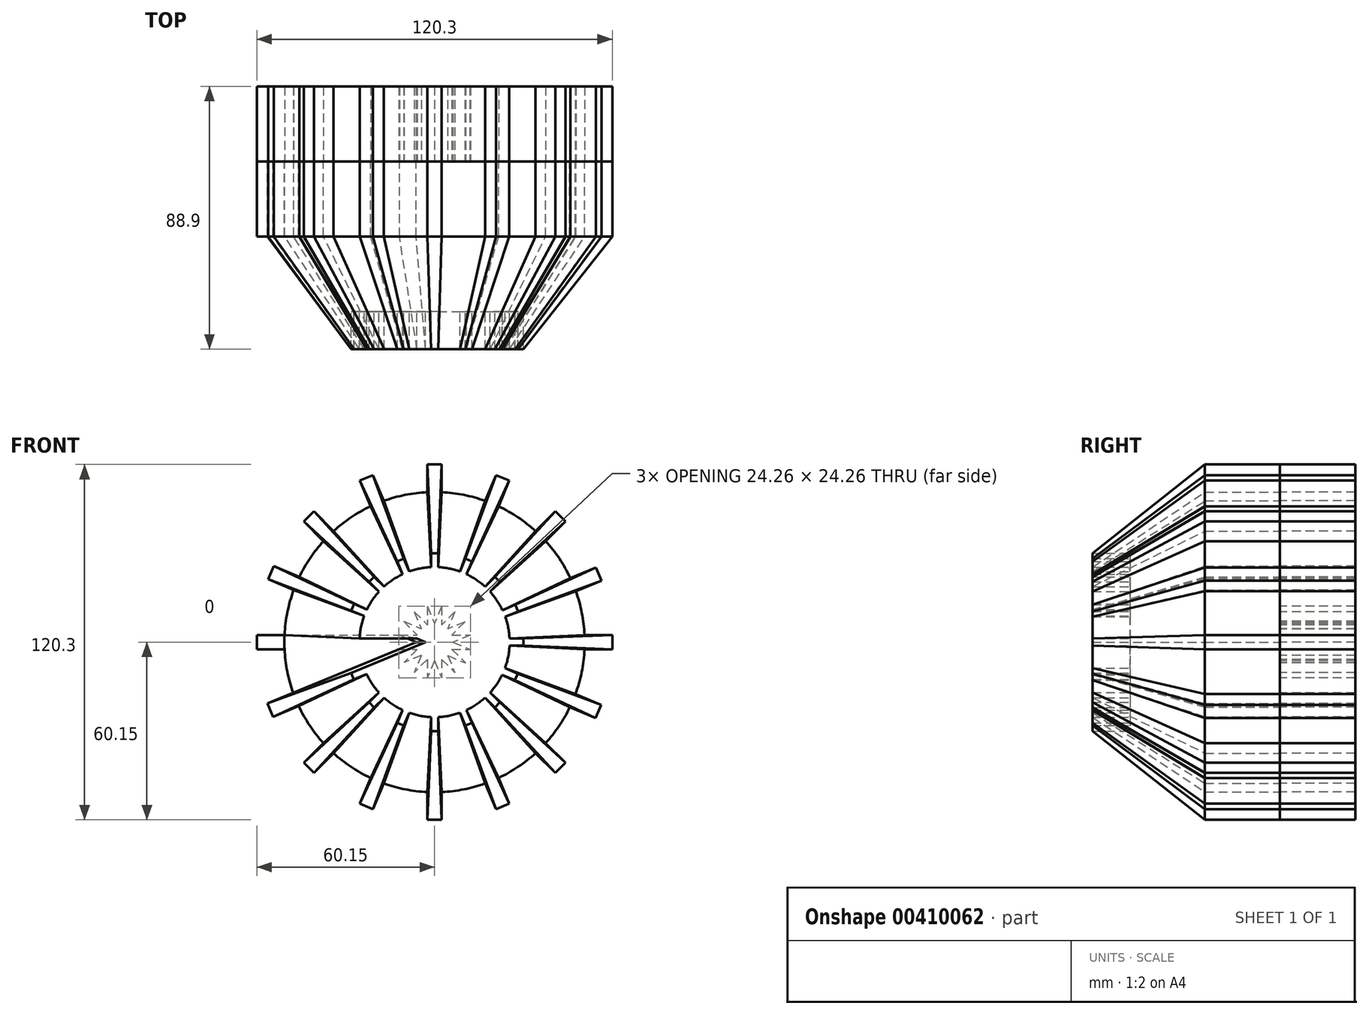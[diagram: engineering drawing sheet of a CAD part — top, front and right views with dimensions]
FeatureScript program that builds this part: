
annotation { "Feature Type Name" : "Feature", "Feature Type Description" : "" }
export const myFeature = defineFeature(function(context is Context, id is Id, definition is map)
    precondition{}
    {
        {
            var Q0;
            Q0=qCreatedBy(makeId("Front.planeOp"),FACE);
            var sketch = newSketch(context, id + "F0", { "sketchPlane" : qUnion([Q0])});
            skCircle(sketch, "E0", {"center": v(0, 0) * mm, "radius": 50.8 * mm});
            skLineSegment(sketch, "E1.bottom", {"start": v(-60.15, 2.41) * mm, "end": v(60.15, 2.41) * mm});
            skLineSegment(sketch, "E1.top", {"start": v(-60.15, -2.41) * mm, "end": v(60.15, -2.41) * mm});
            skLineSegment(sketch, "E1.left", {"start": v(-60.15, 2.41) * mm, "end": v(-60.15, -2.41) * mm});
            skLineSegment(sketch, "E1.right", {"start": v(60.15, 2.41) * mm, "end": v(60.15, -2.41) * mm});
            skLineSegment(sketch, "E2.bottom", {"start": v(2.41, 60.15) * mm, "end": v(2.41, -60.15) * mm});
            skLineSegment(sketch, "E2.top", {"start": v(-2.41, 60.15) * mm, "end": v(-2.41, -60.15) * mm});
            skLineSegment(sketch, "E2.left", {"start": v(2.41, 60.15) * mm, "end": v(-2.41, 60.15) * mm});
            skLineSegment(sketch, "E2.right", {"start": v(2.41, -60.15) * mm, "end": v(-2.41, -60.15) * mm});
            skLineSegment(sketch, "E3.bottom", {"start": v(-20.79, 56.5) * mm, "end": v(25.25, -54.65) * mm});
            skLineSegment(sketch, "E3.top", {"start": v(-25.25, 54.65) * mm, "end": v(20.79, -56.5) * mm});
            skLineSegment(sketch, "E3.left", {"start": v(-20.79, 56.5) * mm, "end": v(-25.25, 54.65) * mm});
            skLineSegment(sketch, "E3.right", {"start": v(25.25, -54.65) * mm, "end": v(20.79, -56.5) * mm});
            skLineSegment(sketch, "E4.bottom", {"start": v(-40.82, 44.24) * mm, "end": v(44.24, -40.82) * mm});
            skLineSegment(sketch, "E4.top", {"start": v(-44.24, 40.82) * mm, "end": v(40.82, -44.24) * mm});
            skLineSegment(sketch, "E4.left", {"start": v(-40.82, 44.24) * mm, "end": v(-44.24, 40.82) * mm});
            skLineSegment(sketch, "E4.right", {"start": v(44.24, -40.82) * mm, "end": v(40.82, -44.24) * mm});
            skLineSegment(sketch, "E5.bottom", {"start": v(-54.42, 25.73) * mm, "end": v(56.3, -21.28) * mm});
            skLineSegment(sketch, "E5.top", {"start": v(-56.3, 21.28) * mm, "end": v(54.42, -25.73) * mm});
            skLineSegment(sketch, "E5.left", {"start": v(-54.42, 25.73) * mm, "end": v(-56.3, 21.28) * mm});
            skLineSegment(sketch, "E5.right", {"start": v(56.3, -21.28) * mm, "end": v(54.42, -25.73) * mm});
            skLineSegment(sketch, "E6.bottom", {"start": v(56.5, 20.8) * mm, "end": v(-54.64, -25.25) * mm});
            skLineSegment(sketch, "E6.top", {"start": v(54.64, 25.25) * mm, "end": v(-56.5, -20.8) * mm});
            skLineSegment(sketch, "E6.left", {"start": v(56.5, 20.8) * mm, "end": v(54.64, 25.25) * mm});
            skLineSegment(sketch, "E6.right", {"start": v(-54.64, -25.25) * mm, "end": v(-56.5, -20.8) * mm});
            skLineSegment(sketch, "E7.bottom", {"start": v(44.24, 40.82) * mm, "end": v(-40.82, -44.24) * mm});
            skLineSegment(sketch, "E7.top", {"start": v(40.82, 44.24) * mm, "end": v(-44.24, -40.82) * mm});
            skLineSegment(sketch, "E7.left", {"start": v(44.24, 40.82) * mm, "end": v(40.82, 44.24) * mm});
            skLineSegment(sketch, "E7.right", {"start": v(-40.82, -44.24) * mm, "end": v(-44.24, -40.82) * mm});
            skLineSegment(sketch, "E8.bottom", {"start": v(25.25, 54.65) * mm, "end": v(-20.79, -56.5) * mm});
            skLineSegment(sketch, "E8.top", {"start": v(20.79, 56.5) * mm, "end": v(-25.25, -54.65) * mm});
            skLineSegment(sketch, "E8.left", {"start": v(25.25, 54.65) * mm, "end": v(20.79, 56.5) * mm});
            skLineSegment(sketch, "E8.right", {"start": v(-20.79, -56.5) * mm, "end": v(-25.25, -54.65) * mm});
            skSolve(sketch);
        }
        {
            var Q0;
            Q0=qCreatedBy(makeId("Front.planeOp"),FACE);
            cPlane(context, id + "F1", {"entities" : qUnion([Q0]), "cplaneType" : CPlaneType.OFFSET, "offset" : 60.16 * mm, "width" : 152.4 * mm, "height" : 152.4 * mm});
        }
        {
            var Q0;
            {var subQ0=sQuery(id+"F0.wireOp",EDGE,"E7.bottom");var subQ1=sQuery(id+"F0.wireOp",EDGE,"E0");var subQ2=makeQuery(id+"F0.imprint","INTERSECT",VERTEX,{"disambiguationData":[OD(1.0)],"derivedFrom":[subQ1,subQ0]});Q0=makeQuery(id+"F0.imprint","IMPRINT",FACE,{"disambiguationData":[TD([[makeQuery(id+"F0.imprint","IMPRINT",EDGE,{"disambiguationData":[TD([[subQ2,-1.0]])],"derivedFrom":subQ1}),1.0]])]});}
            var Q1;
            {var subQ0=sQuery(id+"F0.wireOp",EDGE,"E7.top");var subQ1=sQuery(id+"F0.wireOp",EDGE,"E2.bottom");var subQ2=makeQuery(id+"F0.imprint","INTERSECT",VERTEX,{"derivedFrom":[subQ1,subQ0]});Q1=makeQuery(id+"F0.imprint","IMPRINT",FACE,{"disambiguationData":[TD([[makeQuery(id+"F0.imprint","IMPRINT",EDGE,{"disambiguationData":[TD([[subQ2,-1.0]])],"derivedFrom":subQ1}),1.0]])]});}
            var Q2;
            {var subQ3=sQuery(id+"F0.wireOp",EDGE,"E8.top");var subQ6=sQuery(id+"F0.wireOp",EDGE,"E0");var subQ9=makeQuery(id+"F0.imprint","INTERSECT",VERTEX,{"disambiguationData":[OD(1.0)],"derivedFrom":[subQ6,subQ3]});Q2=makeQuery(id+"F0.imprint","IMPRINT",FACE,{"disambiguationData":[TD([[makeQuery(id+"F0.imprint","IMPRINT",EDGE,{"disambiguationData":[TD([[subQ9,-1.0]])],"derivedFrom":subQ6}),1.0]])]});}
            var Q3;
            {var subQ0=sQuery(id+"F0.wireOp",EDGE,"E3.bottom");var subQ1=sQuery(id+"F0.wireOp",EDGE,"E0");var subQ2=makeQuery(id+"F0.imprint","INTERSECT",VERTEX,{"disambiguationData":[OD(1.0)],"derivedFrom":[subQ1,subQ0]});Q3=makeQuery(id+"F0.imprint","IMPRINT",FACE,{"disambiguationData":[TD([[makeQuery(id+"F0.imprint","IMPRINT",EDGE,{"disambiguationData":[TD([[subQ2,-1.0]])],"derivedFrom":subQ1}),1.0]])]});}
            var Q4;
            {var subQ1=sQuery(id+"F0.wireOp",EDGE,"E0");var subQ7=sQuery(id+"F0.wireOp",EDGE,"E4.top");var subQ9=makeQuery(id+"F0.imprint","INTERSECT",VERTEX,{"disambiguationData":[OD(1.0)],"derivedFrom":[subQ1,subQ7]});Q4=makeQuery(id+"F0.imprint","IMPRINT",FACE,{"disambiguationData":[TD([[makeQuery(id+"F0.imprint","IMPRINT",EDGE,{"disambiguationData":[TD([[subQ9,-1.0]])],"derivedFrom":subQ1}),1.0]])]});}
            var Q5;
            {var subQ0=sQuery(id+"F0.wireOp",EDGE,"E8.bottom");var subQ1=sQuery(id+"F0.wireOp",EDGE,"E0");var subQ2=makeQuery(id+"F0.imprint","INTERSECT",VERTEX,{"disambiguationData":[OD(1.0)],"derivedFrom":[subQ1,subQ0]});Q5=makeQuery(id+"F0.imprint","IMPRINT",FACE,{"disambiguationData":[TD([[makeQuery(id+"F0.imprint","IMPRINT",EDGE,{"disambiguationData":[TD([[subQ2,-1.0]])],"derivedFrom":subQ1}),1.0]])]});}
            var Q6;
            {var subQ5=sQuery(id+"F0.wireOp",EDGE,"E2.top");var subQ6=sQuery(id+"F0.wireOp",EDGE,"E0");var subQ7=makeQuery(id+"F0.imprint","INTERSECT",VERTEX,{"disambiguationData":[OD(1.0)],"derivedFrom":[subQ6,subQ5]});Q6=makeQuery(id+"F0.imprint","IMPRINT",FACE,{"disambiguationData":[TD([[makeQuery(id+"F0.imprint","IMPRINT",EDGE,{"disambiguationData":[TD([[subQ7,-1.0]])],"derivedFrom":subQ6}),1.0]])]});}
            var Q7;
            {var subQ0=sQuery(id+"F0.wireOp",EDGE,"E4.bottom");var subQ1=sQuery(id+"F0.wireOp",EDGE,"E0");var subQ2=makeQuery(id+"F0.imprint","INTERSECT",VERTEX,{"disambiguationData":[OD(1.0)],"derivedFrom":[subQ1,subQ0]});Q7=makeQuery(id+"F0.imprint","IMPRINT",FACE,{"disambiguationData":[TD([[makeQuery(id+"F0.imprint","IMPRINT",EDGE,{"disambiguationData":[TD([[subQ2,-1.0]])],"derivedFrom":subQ1}),1.0]])]});}
            var Q8;
            {var subQ1=sQuery(id+"F0.wireOp",EDGE,"E0");var subQ7=sQuery(id+"F0.wireOp",EDGE,"E5.top");var subQ9=makeQuery(id+"F0.imprint","INTERSECT",VERTEX,{"disambiguationData":[OD(1.0)],"derivedFrom":[subQ1,subQ7]});Q8=makeQuery(id+"F0.imprint","IMPRINT",FACE,{"disambiguationData":[TD([[makeQuery(id+"F0.imprint","IMPRINT",EDGE,{"disambiguationData":[TD([[subQ9,-1.0]])],"derivedFrom":subQ1}),1.0]])]});}
            var Q9;
            {var subQ0=sQuery(id+"F0.wireOp",EDGE,"E6.bottom");var subQ1=sQuery(id+"F0.wireOp",EDGE,"E2.top");var subQ2=makeQuery(id+"F0.imprint","INTERSECT",VERTEX,{"derivedFrom":[subQ1,subQ0]});Q9=makeQuery(id+"F0.imprint","IMPRINT",FACE,{"disambiguationData":[TD([[makeQuery(id+"F0.imprint","IMPRINT",EDGE,{"disambiguationData":[TD([[subQ2,-1.0]])],"derivedFrom":subQ1}),-1.0]])]});}
            var Q10;
            {var subQ0=sQuery(id+"F0.wireOp",EDGE,"E2.bottom");var subQ1=sQuery(id+"F0.wireOp",EDGE,"E0");var subQ2=makeQuery(id+"F0.imprint","INTERSECT",VERTEX,{"disambiguationData":[OD(1.0)],"derivedFrom":[subQ1,subQ0]});Q10=makeQuery(id+"F0.imprint","IMPRINT",FACE,{"disambiguationData":[TD([[makeQuery(id+"F0.imprint","IMPRINT",EDGE,{"disambiguationData":[TD([[subQ2,-1.0]])],"derivedFrom":subQ1}),1.0]])]});}
            var Q11;
            {var subQ0=sQuery(id+"F0.wireOp",EDGE,"E3.top");var subQ1=sQuery(id+"F0.wireOp",EDGE,"E0");var subQ2=makeQuery(id+"F0.imprint","INTERSECT",VERTEX,{"disambiguationData":[OD(1.0)],"derivedFrom":[subQ1,subQ0]});Q11=makeQuery(id+"F0.imprint","IMPRINT",FACE,{"disambiguationData":[TD([[makeQuery(id+"F0.imprint","IMPRINT",EDGE,{"disambiguationData":[TD([[subQ2,-1.0]])],"derivedFrom":subQ1}),1.0]])]});}
            var Q12;
            {var subQ0=sQuery(id+"F0.wireOp",EDGE,"E6.bottom");var subQ1=sQuery(id+"F0.wireOp",EDGE,"E0");var subQ2=makeQuery(id+"F0.imprint","INTERSECT",VERTEX,{"disambiguationData":[OD(0.0)],"derivedFrom":[subQ1,subQ0]});Q12=makeQuery(id+"F0.imprint","IMPRINT",FACE,{"disambiguationData":[TD([[makeQuery(id+"F0.imprint","IMPRINT",EDGE,{"disambiguationData":[TD([[subQ2,1.0]])],"derivedFrom":subQ1}),1.0]])]});}
            var Q13;
            {var subQ1=sQuery(id+"F0.wireOp",EDGE,"E0");var subQ5=sQuery(id+"F0.wireOp",EDGE,"E6.bottom");var subQ6=makeQuery(id+"F0.imprint","INTERSECT",VERTEX,{"disambiguationData":[OD(0.0)],"derivedFrom":[subQ1,subQ5]});Q13=makeQuery(id+"F0.imprint","IMPRINT",FACE,{"disambiguationData":[TD([[makeQuery(id+"F0.imprint","IMPRINT",EDGE,{"disambiguationData":[TD([[subQ6,-1.0]])],"derivedFrom":subQ1}),1.0]])]});}
            var Q14;
            {var subQ0=sQuery(id+"F0.wireOp",EDGE,"E6.top");var subQ1=sQuery(id+"F0.wireOp",EDGE,"E0");var subQ2=makeQuery(id+"F0.imprint","INTERSECT",VERTEX,{"disambiguationData":[OD(0.0)],"derivedFrom":[subQ1,subQ0]});Q14=makeQuery(id+"F0.imprint","IMPRINT",FACE,{"disambiguationData":[TD([[makeQuery(id+"F0.imprint","IMPRINT",EDGE,{"disambiguationData":[TD([[subQ2,-1.0]])],"derivedFrom":subQ1}),1.0]])]});}
            var Q15;
            {var subQ0=sQuery(id+"F0.wireOp",EDGE,"E7.bottom");var subQ1=sQuery(id+"F0.wireOp",EDGE,"E0");var subQ2=makeQuery(id+"F0.imprint","INTERSECT",VERTEX,{"disambiguationData":[OD(0.0)],"derivedFrom":[subQ1,subQ0]});Q15=makeQuery(id+"F0.imprint","IMPRINT",FACE,{"disambiguationData":[TD([[makeQuery(id+"F0.imprint","IMPRINT",EDGE,{"disambiguationData":[TD([[subQ2,-1.0]])],"derivedFrom":subQ1}),1.0]])]});}
            var Q16;
            {var subQ0=sQuery(id+"F0.wireOp",EDGE,"E5.top");var subQ1=sQuery(id+"F0.wireOp",EDGE,"E2.bottom");var subQ2=makeQuery(id+"F0.imprint","INTERSECT",VERTEX,{"derivedFrom":[subQ1,subQ0]});Q16=makeQuery(id+"F0.imprint","IMPRINT",FACE,{"disambiguationData":[TD([[makeQuery(id+"F0.imprint","IMPRINT",EDGE,{"disambiguationData":[TD([[subQ2,-1.0]])],"derivedFrom":subQ1}),1.0]])]});}
            var Q17;
            {var subQ0=sQuery(id+"F0.wireOp",EDGE,"E7.top");var subQ1=sQuery(id+"F0.wireOp",EDGE,"E0");var subQ2=makeQuery(id+"F0.imprint","INTERSECT",VERTEX,{"disambiguationData":[OD(0.0)],"derivedFrom":[subQ1,subQ0]});Q17=makeQuery(id+"F0.imprint","IMPRINT",FACE,{"disambiguationData":[TD([[makeQuery(id+"F0.imprint","IMPRINT",EDGE,{"disambiguationData":[TD([[subQ2,-1.0]])],"derivedFrom":subQ1}),1.0]])]});}
            var Q18;
            {var subQ3=sQuery(id+"F0.wireOp",EDGE,"E8.bottom");var subQ5=sQuery(id+"F0.wireOp",EDGE,"E0");var subQ6=makeQuery(id+"F0.imprint","INTERSECT",VERTEX,{"disambiguationData":[OD(0.0)],"derivedFrom":[subQ5,subQ3]});Q18=makeQuery(id+"F0.imprint","IMPRINT",FACE,{"disambiguationData":[TD([[makeQuery(id+"F0.imprint","IMPRINT",EDGE,{"disambiguationData":[TD([[subQ6,-1.0]])],"derivedFrom":subQ5}),1.0]])]});}
            var Q19;
            {var subQ0=sQuery(id+"F0.wireOp",EDGE,"E8.top");var subQ1=sQuery(id+"F0.wireOp",EDGE,"E0");var subQ2=makeQuery(id+"F0.imprint","INTERSECT",VERTEX,{"disambiguationData":[OD(0.0)],"derivedFrom":[subQ1,subQ0]});Q19=makeQuery(id+"F0.imprint","IMPRINT",FACE,{"disambiguationData":[TD([[makeQuery(id+"F0.imprint","IMPRINT",EDGE,{"disambiguationData":[TD([[subQ2,-1.0]])],"derivedFrom":subQ1}),1.0]])]});}
            var Q20;
            {var subQ0=sQuery(id+"F0.wireOp",EDGE,"E7.bottom");var subQ1=sQuery(id+"F0.wireOp",EDGE,"E1.bottom");var subQ2=makeQuery(id+"F0.imprint","INTERSECT",VERTEX,{"derivedFrom":[subQ1,subQ0]});Q20=makeQuery(id+"F0.imprint","IMPRINT",FACE,{"disambiguationData":[TD([[makeQuery(id+"F0.imprint","IMPRINT",EDGE,{"disambiguationData":[TD([[subQ2,-1.0]])],"derivedFrom":subQ1}),-1.0]])]});}
            var Q21;
            {var subQ5=sQuery(id+"F0.wireOp",EDGE,"E2.bottom");var subQ6=sQuery(id+"F0.wireOp",EDGE,"E0");var subQ7=makeQuery(id+"F0.imprint","INTERSECT",VERTEX,{"disambiguationData":[OD(0.0)],"derivedFrom":[subQ6,subQ5]});Q21=makeQuery(id+"F0.imprint","IMPRINT",FACE,{"disambiguationData":[TD([[makeQuery(id+"F0.imprint","IMPRINT",EDGE,{"disambiguationData":[TD([[subQ7,-1.0]])],"derivedFrom":subQ6}),1.0]])]});}
            var Q22;
            {var subQ0=sQuery(id+"F0.wireOp",EDGE,"E2.top");var subQ1=sQuery(id+"F0.wireOp",EDGE,"E0");var subQ2=makeQuery(id+"F0.imprint","INTERSECT",VERTEX,{"disambiguationData":[OD(0.0)],"derivedFrom":[subQ1,subQ0]});Q22=makeQuery(id+"F0.imprint","IMPRINT",FACE,{"disambiguationData":[TD([[makeQuery(id+"F0.imprint","IMPRINT",EDGE,{"disambiguationData":[TD([[subQ2,-1.0]])],"derivedFrom":subQ1}),1.0]])]});}
            var Q23;
            {var subQ0=sQuery(id+"F0.wireOp",EDGE,"E6.top");var subQ1=sQuery(id+"F0.wireOp",EDGE,"E1.top");var subQ2=makeQuery(id+"F0.imprint","INTERSECT",VERTEX,{"derivedFrom":[subQ1,subQ0]});Q23=makeQuery(id+"F0.imprint","IMPRINT",FACE,{"disambiguationData":[TD([[makeQuery(id+"F0.imprint","IMPRINT",EDGE,{"disambiguationData":[TD([[subQ2,-1.0]])],"derivedFrom":subQ1}),1.0]])]});}
            var Q24;
            {var subQ0=sQuery(id+"F0.wireOp",EDGE,"E3.bottom");var subQ1=sQuery(id+"F0.wireOp",EDGE,"E0");var subQ2=makeQuery(id+"F0.imprint","INTERSECT",VERTEX,{"disambiguationData":[OD(0.0)],"derivedFrom":[subQ1,subQ0]});Q24=makeQuery(id+"F0.imprint","IMPRINT",FACE,{"disambiguationData":[TD([[makeQuery(id+"F0.imprint","IMPRINT",EDGE,{"disambiguationData":[TD([[subQ2,-1.0]])],"derivedFrom":subQ1}),1.0]])]});}
            var Q25;
            {var subQ0=sQuery(id+"F0.wireOp",EDGE,"E3.top");var subQ1=sQuery(id+"F0.wireOp",EDGE,"E0");var subQ2=makeQuery(id+"F0.imprint","INTERSECT",VERTEX,{"disambiguationData":[OD(0.0)],"derivedFrom":[subQ1,subQ0]});Q25=makeQuery(id+"F0.imprint","IMPRINT",FACE,{"disambiguationData":[TD([[makeQuery(id+"F0.imprint","IMPRINT",EDGE,{"disambiguationData":[TD([[subQ2,-1.0]])],"derivedFrom":subQ1}),1.0]])]});}
            var Q26;
            {var subQ1=sQuery(id+"F0.wireOp",EDGE,"E0");var subQ5=sQuery(id+"F0.wireOp",EDGE,"E4.bottom");var subQ9=makeQuery(id+"F0.imprint","INTERSECT",VERTEX,{"disambiguationData":[OD(0.0)],"derivedFrom":[subQ1,subQ5]});Q26=makeQuery(id+"F0.imprint","IMPRINT",FACE,{"disambiguationData":[TD([[makeQuery(id+"F0.imprint","IMPRINT",EDGE,{"disambiguationData":[TD([[subQ9,-1.0]])],"derivedFrom":subQ1}),1.0]])]});}
            var Q27;
            {var subQ0=sQuery(id+"F0.wireOp",EDGE,"E4.bottom");var subQ1=sQuery(id+"F0.wireOp",EDGE,"E2.top");var subQ2=makeQuery(id+"F0.imprint","INTERSECT",VERTEX,{"derivedFrom":[subQ1,subQ0]});Q27=makeQuery(id+"F0.imprint","IMPRINT",FACE,{"disambiguationData":[TD([[makeQuery(id+"F0.imprint","IMPRINT",EDGE,{"disambiguationData":[TD([[subQ2,-1.0]])],"derivedFrom":subQ1}),-1.0]])]});}
            var Q28;
            {var subQ0=sQuery(id+"F0.wireOp",EDGE,"E3.bottom");var subQ1=sQuery(id+"F0.wireOp",EDGE,"E1.top");var subQ2=makeQuery(id+"F0.imprint","INTERSECT",VERTEX,{"derivedFrom":[subQ1,subQ0]});Q28=makeQuery(id+"F0.imprint","IMPRINT",FACE,{"disambiguationData":[TD([[makeQuery(id+"F0.imprint","IMPRINT",EDGE,{"disambiguationData":[TD([[subQ2,-1.0]])],"derivedFrom":subQ1}),-1.0]])]});}
            var Q29;
            {var subQ0=sQuery(id+"F0.wireOp",EDGE,"E7.top");var subQ1=sQuery(id+"F0.wireOp",EDGE,"E1.top");var subQ2=makeQuery(id+"F0.imprint","INTERSECT",VERTEX,{"derivedFrom":[subQ1,subQ0]});Q29=makeQuery(id+"F0.imprint","IMPRINT",FACE,{"disambiguationData":[TD([[makeQuery(id+"F0.imprint","IMPRINT",EDGE,{"disambiguationData":[TD([[subQ2,-1.0]])],"derivedFrom":subQ1}),-1.0]])]});}
            var Q30;
            {var subQ0=sQuery(id+"F0.wireOp",EDGE,"E5.bottom");var subQ1=sQuery(id+"F0.wireOp",EDGE,"E0");var subQ2=makeQuery(id+"F0.imprint","INTERSECT",VERTEX,{"disambiguationData":[OD(0.0)],"derivedFrom":[subQ1,subQ0]});Q30=makeQuery(id+"F0.imprint","IMPRINT",FACE,{"disambiguationData":[TD([[makeQuery(id+"F0.imprint","IMPRINT",EDGE,{"disambiguationData":[TD([[subQ2,-1.0]])],"derivedFrom":subQ1}),1.0]])]});}
            var Q31;
            {var subQ0=sQuery(id+"F0.wireOp",EDGE,"E4.top");var subQ1=sQuery(id+"F0.wireOp",EDGE,"E0");var subQ2=makeQuery(id+"F0.imprint","INTERSECT",VERTEX,{"disambiguationData":[OD(0.0)],"derivedFrom":[subQ1,subQ0]});Q31=makeQuery(id+"F0.imprint","IMPRINT",FACE,{"disambiguationData":[TD([[makeQuery(id+"F0.imprint","IMPRINT",EDGE,{"disambiguationData":[TD([[subQ2,-1.0]])],"derivedFrom":subQ1}),1.0]])]});}
            var Q32;
            {var subQ5=sQuery(id+"F0.wireOp",EDGE,"E1.right");Q32=makeQuery(id+"F0.imprint","IMPRINT",FACE,{"disambiguationData":[TD([[makeQuery(id+"F0.imprint","IMPRINT",EDGE,{"derivedFrom":subQ5}),-1.0]])]});}
            var Q33;
            {var subQ5=sQuery(id+"F0.wireOp",EDGE,"E4.right");Q33=makeQuery(id+"F0.imprint","IMPRINT",FACE,{"disambiguationData":[TD([[makeQuery(id+"F0.imprint","IMPRINT",EDGE,{"derivedFrom":subQ5}),-1.0]])]});}
            var Q34;
            {var subQ5=sQuery(id+"F0.wireOp",EDGE,"E5.right");Q34=makeQuery(id+"F0.imprint","IMPRINT",FACE,{"disambiguationData":[TD([[makeQuery(id+"F0.imprint","IMPRINT",EDGE,{"derivedFrom":subQ5}),-1.0]])]});}
            var Q35;
            {var subQ5=sQuery(id+"F0.wireOp",EDGE,"E6.left");Q35=makeQuery(id+"F0.imprint","IMPRINT",FACE,{"disambiguationData":[TD([[makeQuery(id+"F0.imprint","IMPRINT",EDGE,{"derivedFrom":subQ5}),1.0]])]});}
            var Q36;
            {var subQ5=sQuery(id+"F0.wireOp",EDGE,"E7.left");Q36=makeQuery(id+"F0.imprint","IMPRINT",FACE,{"disambiguationData":[TD([[makeQuery(id+"F0.imprint","IMPRINT",EDGE,{"derivedFrom":subQ5}),1.0]])]});}
            var Q37;
            {var subQ5=sQuery(id+"F0.wireOp",EDGE,"E8.left");Q37=makeQuery(id+"F0.imprint","IMPRINT",FACE,{"disambiguationData":[TD([[makeQuery(id+"F0.imprint","IMPRINT",EDGE,{"derivedFrom":subQ5}),1.0]])]});}
            var Q38;
            {var subQ5=sQuery(id+"F0.wireOp",EDGE,"E2.left");Q38=makeQuery(id+"F0.imprint","IMPRINT",FACE,{"disambiguationData":[TD([[makeQuery(id+"F0.imprint","IMPRINT",EDGE,{"derivedFrom":subQ5}),1.0]])]});}
            var Q39;
            {var subQ5=sQuery(id+"F0.wireOp",EDGE,"E3.left");Q39=makeQuery(id+"F0.imprint","IMPRINT",FACE,{"disambiguationData":[TD([[makeQuery(id+"F0.imprint","IMPRINT",EDGE,{"derivedFrom":subQ5}),1.0]])]});}
            var Q40;
            {var subQ5=sQuery(id+"F0.wireOp",EDGE,"E4.left");Q40=makeQuery(id+"F0.imprint","IMPRINT",FACE,{"disambiguationData":[TD([[makeQuery(id+"F0.imprint","IMPRINT",EDGE,{"derivedFrom":subQ5}),1.0]])]});}
            var Q41;
            {var subQ0=sQuery(id+"F0.wireOp",EDGE,"E1.bottom");var subQ1=sQuery(id+"F0.wireOp",EDGE,"E0");var subQ2=makeQuery(id+"F0.imprint","INTERSECT",VERTEX,{"disambiguationData":[OD(1.0)],"derivedFrom":[subQ1,subQ0]});Q41=makeQuery(id+"F0.imprint","IMPRINT",FACE,{"disambiguationData":[TD([[makeQuery(id+"F0.imprint","IMPRINT",EDGE,{"disambiguationData":[TD([[subQ2,-1.0]])],"derivedFrom":subQ1}),1.0]])]});}
            var Q42;
            {var subQ5=sQuery(id+"F0.wireOp",EDGE,"E5.left");Q42=makeQuery(id+"F0.imprint","IMPRINT",FACE,{"disambiguationData":[TD([[makeQuery(id+"F0.imprint","IMPRINT",EDGE,{"derivedFrom":subQ5}),1.0]])]});}
            var Q43;
            {var subQ5=sQuery(id+"F0.wireOp",EDGE,"E1.left");Q43=makeQuery(id+"F0.imprint","IMPRINT",FACE,{"disambiguationData":[TD([[makeQuery(id+"F0.imprint","IMPRINT",EDGE,{"derivedFrom":subQ5}),1.0]])]});}
            var Q44;
            {var subQ5=sQuery(id+"F0.wireOp",EDGE,"E6.right");Q44=makeQuery(id+"F0.imprint","IMPRINT",FACE,{"disambiguationData":[TD([[makeQuery(id+"F0.imprint","IMPRINT",EDGE,{"derivedFrom":subQ5}),-1.0]])]});}
            var Q45;
            {var subQ5=sQuery(id+"F0.wireOp",EDGE,"E7.right");Q45=makeQuery(id+"F0.imprint","IMPRINT",FACE,{"disambiguationData":[TD([[makeQuery(id+"F0.imprint","IMPRINT",EDGE,{"derivedFrom":subQ5}),-1.0]])]});}
            var Q46;
            {var subQ5=sQuery(id+"F0.wireOp",EDGE,"E8.right");Q46=makeQuery(id+"F0.imprint","IMPRINT",FACE,{"disambiguationData":[TD([[makeQuery(id+"F0.imprint","IMPRINT",EDGE,{"derivedFrom":subQ5}),-1.0]])]});}
            var Q47;
            {var subQ5=sQuery(id+"F0.wireOp",EDGE,"E2.right");Q47=makeQuery(id+"F0.imprint","IMPRINT",FACE,{"disambiguationData":[TD([[makeQuery(id+"F0.imprint","IMPRINT",EDGE,{"derivedFrom":subQ5}),-1.0]])]});}
            var Q48;
            {var subQ5=sQuery(id+"F0.wireOp",EDGE,"E3.right");Q48=makeQuery(id+"F0.imprint","IMPRINT",FACE,{"disambiguationData":[TD([[makeQuery(id+"F0.imprint","IMPRINT",EDGE,{"derivedFrom":subQ5}),-1.0]])]});}
            var Q49;
            {var subQ0=sQuery(id+"F0.wireOp",EDGE,"E5.top");var subQ1=sQuery(id+"F0.wireOp",EDGE,"E0");var subQ2=makeQuery(id+"F0.imprint","INTERSECT",VERTEX,{"disambiguationData":[OD(0.0)],"derivedFrom":[subQ1,subQ0]});Q49=makeQuery(id+"F0.imprint","IMPRINT",FACE,{"disambiguationData":[TD([[makeQuery(id+"F0.imprint","IMPRINT",EDGE,{"disambiguationData":[TD([[subQ2,-1.0]])],"derivedFrom":subQ1}),1.0]])]});}
            var Q50;
            {var subQ0=sQuery(id+"F0.wireOp",EDGE,"E1.top");var subQ1=sQuery(id+"F0.wireOp",EDGE,"E0");var subQ2=makeQuery(id+"F0.imprint","INTERSECT",VERTEX,{"disambiguationData":[OD(0.0)],"derivedFrom":[subQ1,subQ0]});Q50=makeQuery(id+"F0.imprint","IMPRINT",FACE,{"disambiguationData":[TD([[makeQuery(id+"F0.imprint","IMPRINT",EDGE,{"disambiguationData":[TD([[subQ2,-1.0]])],"derivedFrom":subQ1}),1.0]])]});}
            var Q51;
            {var subQ0=sQuery(id+"F0.wireOp",EDGE,"E6.top");var subQ1=sQuery(id+"F0.wireOp",EDGE,"E0");var subQ2=makeQuery(id+"F0.imprint","INTERSECT",VERTEX,{"disambiguationData":[OD(1.0)],"derivedFrom":[subQ1,subQ0]});Q51=makeQuery(id+"F0.imprint","IMPRINT",FACE,{"disambiguationData":[TD([[makeQuery(id+"F0.imprint","IMPRINT",EDGE,{"disambiguationData":[TD([[subQ2,-1.0]])],"derivedFrom":subQ1}),1.0]])]});}
            var Q52;
            {var subQ0=sQuery(id+"F0.wireOp",EDGE,"E5.bottom");var subQ1=sQuery(id+"F0.wireOp",EDGE,"E0");var subQ2=makeQuery(id+"F0.imprint","INTERSECT",VERTEX,{"disambiguationData":[OD(1.0)],"derivedFrom":[subQ1,subQ0]});Q52=makeQuery(id+"F0.imprint","IMPRINT",FACE,{"disambiguationData":[TD([[makeQuery(id+"F0.imprint","IMPRINT",EDGE,{"disambiguationData":[TD([[subQ2,-1.0]])],"derivedFrom":subQ1}),1.0]])]});}
            var Q53;
            {var subQ0=sQuery(id+"F0.wireOp",EDGE,"E6.bottom");var subQ1=sQuery(id+"F0.wireOp",EDGE,"E0");var subQ2=makeQuery(id+"F0.imprint","INTERSECT",VERTEX,{"disambiguationData":[OD(1.0)],"derivedFrom":[subQ1,subQ0]});Q53=makeQuery(id+"F0.imprint","IMPRINT",FACE,{"disambiguationData":[TD([[makeQuery(id+"F0.imprint","IMPRINT",EDGE,{"disambiguationData":[TD([[subQ2,-1.0]])],"derivedFrom":subQ1}),1.0]])]});}
            var Q54;
            {var subQ5=sQuery(id+"F0.wireOp",EDGE,"E1.bottom");var subQ6=sQuery(id+"F0.wireOp",EDGE,"E0");var subQ7=makeQuery(id+"F0.imprint","INTERSECT",VERTEX,{"disambiguationData":[OD(0.0)],"derivedFrom":[subQ6,subQ5]});Q54=makeQuery(id+"F0.imprint","IMPRINT",FACE,{"disambiguationData":[TD([[makeQuery(id+"F0.imprint","IMPRINT",EDGE,{"disambiguationData":[TD([[subQ7,1.0]])],"derivedFrom":subQ6}),1.0]])]});}
            var Q55;
            {var subQ0=sQuery(id+"F0.wireOp",EDGE,"E7.bottom");var subQ1=sQuery(id+"F0.wireOp",EDGE,"E2.top");var subQ2=makeQuery(id+"F0.imprint","INTERSECT",VERTEX,{"derivedFrom":[subQ1,subQ0]});Q55=makeQuery(id+"F0.imprint","IMPRINT",FACE,{"disambiguationData":[TD([[makeQuery(id+"F0.imprint","IMPRINT",EDGE,{"disambiguationData":[TD([[subQ2,-1.0]])],"derivedFrom":subQ1}),1.0]])]});}
            var Q56;
            {var subQ0=sQuery(id+"F0.wireOp",EDGE,"E7.top");var subQ1=sQuery(id+"F0.wireOp",EDGE,"E0");var subQ2=makeQuery(id+"F0.imprint","INTERSECT",VERTEX,{"disambiguationData":[OD(1.0)],"derivedFrom":[subQ1,subQ0]});Q56=makeQuery(id+"F0.imprint","IMPRINT",FACE,{"disambiguationData":[TD([[makeQuery(id+"F0.imprint","IMPRINT",EDGE,{"disambiguationData":[TD([[subQ2,-1.0]])],"derivedFrom":subQ1}),1.0]])]});}
            var Q57;
            {var subQ0=sQuery(id+"F0.wireOp",EDGE,"E2.top");var subQ1=sQuery(id+"F0.wireOp",EDGE,"E1.top");var subQ2=makeQuery(id+"F0.imprint","INTERSECT",VERTEX,{"derivedFrom":[subQ1,subQ0]});Q57=makeQuery(id+"F0.imprint","IMPRINT",FACE,{"disambiguationData":[TD([[makeQuery(id+"F0.imprint","IMPRINT",EDGE,{"disambiguationData":[TD([[subQ2,-1.0]])],"derivedFrom":subQ1}),-1.0]])]});}
            var Q58;
            {var subQ0=sQuery(id+"F0.wireOp",EDGE,"E6.bottom");var subQ1=sQuery(id+"F0.wireOp",EDGE,"E2.top");var subQ2=makeQuery(id+"F0.imprint","INTERSECT",VERTEX,{"derivedFrom":[subQ1,subQ0]});Q58=makeQuery(id+"F0.imprint","IMPRINT",FACE,{"disambiguationData":[TD([[makeQuery(id+"F0.imprint","IMPRINT",EDGE,{"disambiguationData":[TD([[subQ2,-1.0]])],"derivedFrom":subQ1}),1.0]])]});}
            var Q59;
            {var subQ0=sQuery(id+"F0.wireOp",EDGE,"E7.bottom");var subQ1=sQuery(id+"F0.wireOp",EDGE,"E4.bottom");var subQ2=makeQuery(id+"F0.imprint","INTERSECT",VERTEX,{"derivedFrom":[subQ1,subQ0]});Q59=makeQuery(id+"F0.imprint","IMPRINT",FACE,{"disambiguationData":[TD([[makeQuery(id+"F0.imprint","IMPRINT",EDGE,{"disambiguationData":[TD([[subQ2,-1.0]])],"derivedFrom":subQ1}),1.0]])]});}
            var Q60;
            {var subQ0=sQuery(id+"F0.wireOp",EDGE,"E6.top");var subQ1=sQuery(id+"F0.wireOp",EDGE,"E4.top");var subQ2=makeQuery(id+"F0.imprint","INTERSECT",VERTEX,{"derivedFrom":[subQ1,subQ0]});Q60=makeQuery(id+"F0.imprint","IMPRINT",FACE,{"disambiguationData":[TD([[makeQuery(id+"F0.imprint","IMPRINT",EDGE,{"disambiguationData":[TD([[subQ2,-1.0]])],"derivedFrom":subQ1}),-1.0]])]});}
            var Q61;
            {var subQ0=sQuery(id+"F0.wireOp",EDGE,"E5.top");var subQ1=sQuery(id+"F0.wireOp",EDGE,"E1.bottom");var subQ2=makeQuery(id+"F0.imprint","INTERSECT",VERTEX,{"derivedFrom":[subQ1,subQ0]});Q61=makeQuery(id+"F0.imprint","IMPRINT",FACE,{"disambiguationData":[TD([[makeQuery(id+"F0.imprint","IMPRINT",EDGE,{"disambiguationData":[TD([[subQ2,-1.0]])],"derivedFrom":subQ1}),-1.0]])]});}
            var Q62;
            {var subQ0=sQuery(id+"F0.wireOp",EDGE,"E8.top");var subQ1=sQuery(id+"F0.wireOp",EDGE,"E3.bottom");var subQ2=makeQuery(id+"F0.imprint","INTERSECT",VERTEX,{"derivedFrom":[subQ1,subQ0]});Q62=makeQuery(id+"F0.imprint","IMPRINT",FACE,{"disambiguationData":[TD([[makeQuery(id+"F0.imprint","IMPRINT",EDGE,{"disambiguationData":[TD([[subQ2,-1.0]])],"derivedFrom":subQ1}),-1.0]])]});}
            var Q63;
            {var subQ0=sQuery(id+"F0.wireOp",EDGE,"E8.bottom");var subQ1=sQuery(id+"F0.wireOp",EDGE,"E1.bottom");var subQ2=makeQuery(id+"F0.imprint","INTERSECT",VERTEX,{"derivedFrom":[subQ1,subQ0]});Q63=makeQuery(id+"F0.imprint","IMPRINT",FACE,{"disambiguationData":[TD([[makeQuery(id+"F0.imprint","IMPRINT",EDGE,{"disambiguationData":[TD([[subQ2,-1.0]])],"derivedFrom":subQ1}),-1.0]])]});}
            var Q64;
            {var subQ0=sQuery(id+"F0.wireOp",EDGE,"E4.top");var subQ1=sQuery(id+"F0.wireOp",EDGE,"E1.bottom");var subQ2=makeQuery(id+"F0.imprint","INTERSECT",VERTEX,{"derivedFrom":[subQ1,subQ0]});Q64=makeQuery(id+"F0.imprint","IMPRINT",FACE,{"disambiguationData":[TD([[makeQuery(id+"F0.imprint","IMPRINT",EDGE,{"disambiguationData":[TD([[subQ2,-1.0]])],"derivedFrom":subQ1}),1.0]])]});}
            var Q65;
            {var subQ0=sQuery(id+"F0.wireOp",EDGE,"E8.bottom");var subQ1=sQuery(id+"F0.wireOp",EDGE,"E1.top");var subQ2=makeQuery(id+"F0.imprint","INTERSECT",VERTEX,{"derivedFrom":[subQ1,subQ0]});Q65=makeQuery(id+"F0.imprint","IMPRINT",FACE,{"disambiguationData":[TD([[makeQuery(id+"F0.imprint","IMPRINT",EDGE,{"disambiguationData":[TD([[subQ2,-1.0]])],"derivedFrom":subQ1}),-1.0]])]});}
            var Q66;
            {var subQ0=sQuery(id+"F0.wireOp",EDGE,"E8.bottom");var subQ1=sQuery(id+"F0.wireOp",EDGE,"E1.bottom");var subQ2=makeQuery(id+"F0.imprint","INTERSECT",VERTEX,{"derivedFrom":[subQ1,subQ0]});Q66=makeQuery(id+"F0.imprint","IMPRINT",FACE,{"disambiguationData":[TD([[makeQuery(id+"F0.imprint","IMPRINT",EDGE,{"disambiguationData":[TD([[subQ2,-1.0]])],"derivedFrom":subQ1}),1.0]])]});}
            var Q67;
            {var subQ0=sQuery(id+"F0.wireOp",EDGE,"E5.top");var subQ1=sQuery(id+"F0.wireOp",EDGE,"E2.bottom");var subQ2=makeQuery(id+"F0.imprint","INTERSECT",VERTEX,{"derivedFrom":[subQ1,subQ0]});Q67=makeQuery(id+"F0.imprint","IMPRINT",FACE,{"disambiguationData":[TD([[makeQuery(id+"F0.imprint","IMPRINT",EDGE,{"disambiguationData":[TD([[subQ2,-1.0]])],"derivedFrom":subQ1}),-1.0]])]});}
            var Q68;
            {var subQ0=sQuery(id+"F0.wireOp",EDGE,"E3.top");var subQ1=sQuery(id+"F0.wireOp",EDGE,"E1.bottom");var subQ2=makeQuery(id+"F0.imprint","INTERSECT",VERTEX,{"derivedFrom":[subQ1,subQ0]});Q68=makeQuery(id+"F0.imprint","IMPRINT",FACE,{"disambiguationData":[TD([[makeQuery(id+"F0.imprint","IMPRINT",EDGE,{"disambiguationData":[TD([[subQ2,-1.0]])],"derivedFrom":subQ1}),1.0]])]});}
            var Q69;
            {var subQ0=sQuery(id+"F0.wireOp",EDGE,"E4.top");var subQ1=sQuery(id+"F0.wireOp",EDGE,"E2.bottom");var subQ2=makeQuery(id+"F0.imprint","INTERSECT",VERTEX,{"derivedFrom":[subQ1,subQ0]});Q69=makeQuery(id+"F0.imprint","IMPRINT",FACE,{"disambiguationData":[TD([[makeQuery(id+"F0.imprint","IMPRINT",EDGE,{"disambiguationData":[TD([[subQ2,-1.0]])],"derivedFrom":subQ1}),-1.0]])]});}
            var Q70;
            {var subQ0=sQuery(id+"F0.wireOp",EDGE,"E2.bottom");var subQ1=sQuery(id+"F0.wireOp",EDGE,"E1.top");var subQ2=makeQuery(id+"F0.imprint","INTERSECT",VERTEX,{"derivedFrom":[subQ1,subQ0]});Q70=makeQuery(id+"F0.imprint","IMPRINT",FACE,{"disambiguationData":[TD([[makeQuery(id+"F0.imprint","IMPRINT",EDGE,{"disambiguationData":[TD([[subQ2,-1.0]])],"derivedFrom":subQ1}),-1.0]])]});}
            var Q71;
            {var subQ0=sQuery(id+"F0.wireOp",EDGE,"E3.bottom");var subQ1=sQuery(id+"F0.wireOp",EDGE,"E2.top");var subQ2=makeQuery(id+"F0.imprint","INTERSECT",VERTEX,{"derivedFrom":[subQ1,subQ0]});Q71=makeQuery(id+"F0.imprint","IMPRINT",FACE,{"disambiguationData":[TD([[makeQuery(id+"F0.imprint","IMPRINT",EDGE,{"disambiguationData":[TD([[subQ2,-1.0]])],"derivedFrom":subQ1}),1.0]])]});}
            var Q72;
            {var subQ0=sQuery(id+"F0.wireOp",EDGE,"E3.bottom");var subQ1=sQuery(id+"F0.wireOp",EDGE,"E1.top");var subQ2=makeQuery(id+"F0.imprint","INTERSECT",VERTEX,{"derivedFrom":[subQ1,subQ0]});Q72=makeQuery(id+"F0.imprint","IMPRINT",FACE,{"disambiguationData":[TD([[makeQuery(id+"F0.imprint","IMPRINT",EDGE,{"disambiguationData":[TD([[subQ2,-1.0]])],"derivedFrom":subQ1}),1.0]])]});}
            var Q73;
            {var subQ0=sQuery(id+"F0.wireOp",EDGE,"E7.top");var subQ1=sQuery(id+"F0.wireOp",EDGE,"E1.top");var subQ2=makeQuery(id+"F0.imprint","INTERSECT",VERTEX,{"derivedFrom":[subQ1,subQ0]});Q73=makeQuery(id+"F0.imprint","IMPRINT",FACE,{"disambiguationData":[TD([[makeQuery(id+"F0.imprint","IMPRINT",EDGE,{"disambiguationData":[TD([[subQ2,-1.0]])],"derivedFrom":subQ1}),1.0]])]});}
            var Q74;
            {var subQ0=sQuery(id+"F0.wireOp",EDGE,"E4.bottom");var subQ1=sQuery(id+"F0.wireOp",EDGE,"E2.top");var subQ2=makeQuery(id+"F0.imprint","INTERSECT",VERTEX,{"derivedFrom":[subQ1,subQ0]});Q74=makeQuery(id+"F0.imprint","IMPRINT",FACE,{"disambiguationData":[TD([[makeQuery(id+"F0.imprint","IMPRINT",EDGE,{"disambiguationData":[TD([[subQ2,-1.0]])],"derivedFrom":subQ1}),1.0]])]});}
            var Q75;
            {var subQ0=sQuery(id+"F0.wireOp",EDGE,"E8.top");var subQ1=sQuery(id+"F0.wireOp",EDGE,"E1.bottom");var subQ2=makeQuery(id+"F0.imprint","INTERSECT",VERTEX,{"derivedFrom":[subQ1,subQ0]});Q75=makeQuery(id+"F0.imprint","IMPRINT",FACE,{"disambiguationData":[TD([[makeQuery(id+"F0.imprint","IMPRINT",EDGE,{"disambiguationData":[TD([[subQ2,-1.0]])],"derivedFrom":subQ1}),1.0]])]});}
            var Q76;
            {var subQ0=sQuery(id+"F0.wireOp",EDGE,"E4.bottom");var subQ1=sQuery(id+"F0.wireOp",EDGE,"E1.top");var subQ2=makeQuery(id+"F0.imprint","INTERSECT",VERTEX,{"derivedFrom":[subQ1,subQ0]});Q76=makeQuery(id+"F0.imprint","IMPRINT",FACE,{"disambiguationData":[TD([[makeQuery(id+"F0.imprint","IMPRINT",EDGE,{"disambiguationData":[TD([[subQ2,-1.0]])],"derivedFrom":subQ1}),1.0]])]});}
            var Q77;
            {var subQ0=sQuery(id+"F0.wireOp",EDGE,"E8.top");var subQ1=sQuery(id+"F0.wireOp",EDGE,"E4.bottom");var subQ2=makeQuery(id+"F0.imprint","INTERSECT",VERTEX,{"derivedFrom":[subQ1,subQ0]});Q77=makeQuery(id+"F0.imprint","IMPRINT",FACE,{"disambiguationData":[TD([[makeQuery(id+"F0.imprint","IMPRINT",EDGE,{"disambiguationData":[TD([[subQ2,-1.0]])],"derivedFrom":subQ1}),-1.0]])]});}
            var Q78;
            {var subQ0=sQuery(id+"F0.wireOp",EDGE,"E8.top");var subQ1=sQuery(id+"F0.wireOp",EDGE,"E2.bottom");var subQ2=makeQuery(id+"F0.imprint","INTERSECT",VERTEX,{"derivedFrom":[subQ1,subQ0]});Q78=makeQuery(id+"F0.imprint","IMPRINT",FACE,{"disambiguationData":[TD([[makeQuery(id+"F0.imprint","IMPRINT",EDGE,{"disambiguationData":[TD([[subQ2,-1.0]])],"derivedFrom":subQ1}),-1.0]])]});}
            var Q79;
            {var subQ0=sQuery(id+"F0.wireOp",EDGE,"E8.top");var subQ1=sQuery(id+"F0.wireOp",EDGE,"E1.top");var subQ2=makeQuery(id+"F0.imprint","INTERSECT",VERTEX,{"derivedFrom":[subQ1,subQ0]});Q79=makeQuery(id+"F0.imprint","IMPRINT",FACE,{"disambiguationData":[TD([[makeQuery(id+"F0.imprint","IMPRINT",EDGE,{"disambiguationData":[TD([[subQ2,-1.0]])],"derivedFrom":subQ1}),-1.0]])]});}
            var Q80;
            {var subQ0=sQuery(id+"F0.wireOp",EDGE,"E2.bottom");var subQ1=sQuery(id+"F0.wireOp",EDGE,"E1.bottom");var subQ2=makeQuery(id+"F0.imprint","INTERSECT",VERTEX,{"derivedFrom":[subQ1,subQ0]});Q80=makeQuery(id+"F0.imprint","IMPRINT",FACE,{"disambiguationData":[TD([[makeQuery(id+"F0.imprint","IMPRINT",EDGE,{"disambiguationData":[TD([[subQ2,-1.0]])],"derivedFrom":subQ1}),1.0]])]});}
            var Q81;
            {var subQ0=sQuery(id+"F0.wireOp",EDGE,"E7.top");var subQ1=sQuery(id+"F0.wireOp",EDGE,"E2.bottom");var subQ2=makeQuery(id+"F0.imprint","INTERSECT",VERTEX,{"derivedFrom":[subQ1,subQ0]});Q81=makeQuery(id+"F0.imprint","IMPRINT",FACE,{"disambiguationData":[TD([[makeQuery(id+"F0.imprint","IMPRINT",EDGE,{"disambiguationData":[TD([[subQ2,-1.0]])],"derivedFrom":subQ1}),-1.0]])]});}
            var Q82;
            {var subQ0=sQuery(id+"F0.wireOp",EDGE,"E7.bottom");var subQ1=sQuery(id+"F0.wireOp",EDGE,"E4.top");var subQ2=makeQuery(id+"F0.imprint","INTERSECT",VERTEX,{"derivedFrom":[subQ1,subQ0]});Q82=makeQuery(id+"F0.imprint","IMPRINT",FACE,{"disambiguationData":[TD([[makeQuery(id+"F0.imprint","IMPRINT",EDGE,{"disambiguationData":[TD([[subQ2,-1.0]])],"derivedFrom":subQ1}),1.0]])]});}
            var Q83;
            {var subQ0=sQuery(id+"F0.wireOp",EDGE,"E3.bottom");var subQ1=sQuery(id+"F0.wireOp",EDGE,"E1.bottom");var subQ2=makeQuery(id+"F0.imprint","INTERSECT",VERTEX,{"derivedFrom":[subQ1,subQ0]});Q83=makeQuery(id+"F0.imprint","IMPRINT",FACE,{"disambiguationData":[TD([[makeQuery(id+"F0.imprint","IMPRINT",EDGE,{"disambiguationData":[TD([[subQ2,-1.0]])],"derivedFrom":subQ1}),1.0]])]});}
            var Q84;
            {var subQ0=sQuery(id+"F0.wireOp",EDGE,"E7.top");var subQ1=sQuery(id+"F0.wireOp",EDGE,"E4.top");var subQ2=makeQuery(id+"F0.imprint","INTERSECT",VERTEX,{"derivedFrom":[subQ1,subQ0]});Q84=makeQuery(id+"F0.imprint","IMPRINT",FACE,{"disambiguationData":[TD([[makeQuery(id+"F0.imprint","IMPRINT",EDGE,{"disambiguationData":[TD([[subQ2,-1.0]])],"derivedFrom":subQ1}),-1.0]])]});}
            var Q85;
            {var subQ0=sQuery(id+"F0.wireOp",EDGE,"E6.bottom");var subQ1=sQuery(id+"F0.wireOp",EDGE,"E1.top");var subQ2=makeQuery(id+"F0.imprint","INTERSECT",VERTEX,{"derivedFrom":[subQ1,subQ0]});Q85=makeQuery(id+"F0.imprint","IMPRINT",FACE,{"disambiguationData":[TD([[makeQuery(id+"F0.imprint","IMPRINT",EDGE,{"disambiguationData":[TD([[subQ2,-1.0]])],"derivedFrom":subQ1}),-1.0]])]});}
            var Q86;
            {var subQ0=sQuery(id+"F0.wireOp",EDGE,"E7.top");var subQ1=sQuery(id+"F0.wireOp",EDGE,"E3.bottom");var subQ2=makeQuery(id+"F0.imprint","INTERSECT",VERTEX,{"derivedFrom":[subQ1,subQ0]});Q86=makeQuery(id+"F0.imprint","IMPRINT",FACE,{"disambiguationData":[TD([[makeQuery(id+"F0.imprint","IMPRINT",EDGE,{"disambiguationData":[TD([[subQ2,-1.0]])],"derivedFrom":subQ1}),-1.0]])]});}
            var Q87;
            {var subQ0=sQuery(id+"F0.wireOp",EDGE,"E4.top");var subQ1=sQuery(id+"F0.wireOp",EDGE,"E1.bottom");var subQ2=makeQuery(id+"F0.imprint","INTERSECT",VERTEX,{"derivedFrom":[subQ1,subQ0]});Q87=makeQuery(id+"F0.imprint","IMPRINT",FACE,{"disambiguationData":[TD([[makeQuery(id+"F0.imprint","IMPRINT",EDGE,{"disambiguationData":[TD([[subQ2,-1.0]])],"derivedFrom":subQ1}),-1.0]])]});}
            var Q88;
            {var subQ0=sQuery(id+"F0.wireOp",EDGE,"E2.bottom");var subQ1=sQuery(id+"F0.wireOp",EDGE,"E1.top");var subQ2=makeQuery(id+"F0.imprint","INTERSECT",VERTEX,{"derivedFrom":[subQ1,subQ0]});Q88=makeQuery(id+"F0.imprint","IMPRINT",FACE,{"disambiguationData":[TD([[makeQuery(id+"F0.imprint","IMPRINT",EDGE,{"disambiguationData":[TD([[subQ2,-1.0]])],"derivedFrom":subQ1}),1.0]])]});}
            var Q89;
            {var subQ0=sQuery(id+"F0.wireOp",EDGE,"E2.top");var subQ1=sQuery(id+"F0.wireOp",EDGE,"E1.bottom");var subQ2=makeQuery(id+"F0.imprint","INTERSECT",VERTEX,{"derivedFrom":[subQ1,subQ0]});Q89=makeQuery(id+"F0.imprint","IMPRINT",FACE,{"disambiguationData":[TD([[makeQuery(id+"F0.imprint","IMPRINT",EDGE,{"disambiguationData":[TD([[subQ2,-1.0]])],"derivedFrom":subQ1}),1.0]])]});}
            var Q90;
            {var subQ0=sQuery(id+"F0.wireOp",EDGE,"E6.bottom");var subQ1=sQuery(id+"F0.wireOp",EDGE,"E3.top");var subQ2=makeQuery(id+"F0.imprint","INTERSECT",VERTEX,{"derivedFrom":[subQ1,subQ0]});Q90=makeQuery(id+"F0.imprint","IMPRINT",FACE,{"disambiguationData":[TD([[makeQuery(id+"F0.imprint","IMPRINT",EDGE,{"disambiguationData":[TD([[subQ2,-1.0]])],"derivedFrom":subQ1}),1.0]])]});}
            var Q91;
            {var subQ0=sQuery(id+"F0.wireOp",EDGE,"E7.bottom");var subQ1=sQuery(id+"F0.wireOp",EDGE,"E3.top");var subQ2=makeQuery(id+"F0.imprint","INTERSECT",VERTEX,{"derivedFrom":[subQ1,subQ0]});Q91=makeQuery(id+"F0.imprint","IMPRINT",FACE,{"disambiguationData":[TD([[makeQuery(id+"F0.imprint","IMPRINT",EDGE,{"disambiguationData":[TD([[subQ2,-1.0]])],"derivedFrom":subQ1}),1.0]])]});}
            var Q92;
            {var subQ0=sQuery(id+"F0.wireOp",EDGE,"E7.bottom");var subQ1=sQuery(id+"F0.wireOp",EDGE,"E1.top");var subQ2=makeQuery(id+"F0.imprint","INTERSECT",VERTEX,{"derivedFrom":[subQ1,subQ0]});Q92=makeQuery(id+"F0.imprint","IMPRINT",FACE,{"disambiguationData":[TD([[makeQuery(id+"F0.imprint","IMPRINT",EDGE,{"disambiguationData":[TD([[subQ2,-1.0]])],"derivedFrom":subQ1}),-1.0]])]});}
            var Q93;
            {var subQ0=sQuery(id+"F0.wireOp",EDGE,"E4.bottom");var subQ1=sQuery(id+"F0.wireOp",EDGE,"E1.bottom");var subQ2=makeQuery(id+"F0.imprint","INTERSECT",VERTEX,{"derivedFrom":[subQ1,subQ0]});Q93=makeQuery(id+"F0.imprint","IMPRINT",FACE,{"disambiguationData":[TD([[makeQuery(id+"F0.imprint","IMPRINT",EDGE,{"disambiguationData":[TD([[subQ2,-1.0]])],"derivedFrom":subQ1}),1.0]])]});}
            var Q94;
            {var subQ0=sQuery(id+"F0.wireOp",EDGE,"E6.bottom");var subQ1=sQuery(id+"F0.wireOp",EDGE,"E4.top");var subQ2=makeQuery(id+"F0.imprint","INTERSECT",VERTEX,{"derivedFrom":[subQ1,subQ0]});Q94=makeQuery(id+"F0.imprint","IMPRINT",FACE,{"disambiguationData":[TD([[makeQuery(id+"F0.imprint","IMPRINT",EDGE,{"disambiguationData":[TD([[subQ2,-1.0]])],"derivedFrom":subQ1}),1.0]])]});}
            var Q95;
            {var subQ0=sQuery(id+"F0.wireOp",EDGE,"E3.top");var subQ1=sQuery(id+"F0.wireOp",EDGE,"E1.top");var subQ2=makeQuery(id+"F0.imprint","INTERSECT",VERTEX,{"derivedFrom":[subQ1,subQ0]});Q95=makeQuery(id+"F0.imprint","IMPRINT",FACE,{"disambiguationData":[TD([[makeQuery(id+"F0.imprint","IMPRINT",EDGE,{"disambiguationData":[TD([[subQ2,-1.0]])],"derivedFrom":subQ1}),-1.0]])]});}
            var Q96;
            {var subQ0=sQuery(id+"F0.wireOp",EDGE,"E8.bottom");var subQ1=sQuery(id+"F0.wireOp",EDGE,"E1.top");var subQ2=makeQuery(id+"F0.imprint","INTERSECT",VERTEX,{"derivedFrom":[subQ1,subQ0]});Q96=makeQuery(id+"F0.imprint","IMPRINT",FACE,{"disambiguationData":[TD([[makeQuery(id+"F0.imprint","IMPRINT",EDGE,{"disambiguationData":[TD([[subQ2,-1.0]])],"derivedFrom":subQ1}),1.0]])]});}
            var Q97;
            {var subQ0=sQuery(id+"F0.wireOp",EDGE,"E3.top");var subQ1=sQuery(id+"F0.wireOp",EDGE,"E1.bottom");var subQ2=makeQuery(id+"F0.imprint","INTERSECT",VERTEX,{"derivedFrom":[subQ1,subQ0]});Q97=makeQuery(id+"F0.imprint","IMPRINT",FACE,{"disambiguationData":[TD([[makeQuery(id+"F0.imprint","IMPRINT",EDGE,{"disambiguationData":[TD([[subQ2,-1.0]])],"derivedFrom":subQ1}),-1.0]])]});}
            var Q98;
            {var subQ0=sQuery(id+"F0.wireOp",EDGE,"E6.top");var subQ1=sQuery(id+"F0.wireOp",EDGE,"E3.top");var subQ2=makeQuery(id+"F0.imprint","INTERSECT",VERTEX,{"derivedFrom":[subQ1,subQ0]});Q98=makeQuery(id+"F0.imprint","IMPRINT",FACE,{"disambiguationData":[TD([[makeQuery(id+"F0.imprint","IMPRINT",EDGE,{"disambiguationData":[TD([[subQ2,-1.0]])],"derivedFrom":subQ1}),-1.0]])]});}
            var Q99;
            {var subQ0=sQuery(id+"F0.wireOp",EDGE,"E7.top");var subQ1=sQuery(id+"F0.wireOp",EDGE,"E4.bottom");var subQ2=makeQuery(id+"F0.imprint","INTERSECT",VERTEX,{"derivedFrom":[subQ1,subQ0]});Q99=makeQuery(id+"F0.imprint","IMPRINT",FACE,{"disambiguationData":[TD([[makeQuery(id+"F0.imprint","IMPRINT",EDGE,{"disambiguationData":[TD([[subQ2,-1.0]])],"derivedFrom":subQ1}),-1.0]])]});}
            var Q100;
            {var subQ0=sQuery(id+"F0.wireOp",EDGE,"E4.top");var subQ1=sQuery(id+"F0.wireOp",EDGE,"E1.top");var subQ2=makeQuery(id+"F0.imprint","INTERSECT",VERTEX,{"derivedFrom":[subQ1,subQ0]});Q100=makeQuery(id+"F0.imprint","IMPRINT",FACE,{"disambiguationData":[TD([[makeQuery(id+"F0.imprint","IMPRINT",EDGE,{"disambiguationData":[TD([[subQ2,-1.0]])],"derivedFrom":subQ1}),-1.0]])]});}
            var Q101;
            {var subQ0=sQuery(id+"F0.wireOp",EDGE,"E7.top");var subQ1=sQuery(id+"F0.wireOp",EDGE,"E1.bottom");var subQ2=makeQuery(id+"F0.imprint","INTERSECT",VERTEX,{"derivedFrom":[subQ1,subQ0]});Q101=makeQuery(id+"F0.imprint","IMPRINT",FACE,{"disambiguationData":[TD([[makeQuery(id+"F0.imprint","IMPRINT",EDGE,{"disambiguationData":[TD([[subQ2,-1.0]])],"derivedFrom":subQ1}),1.0]])]});}
            var Q102;
            {var subQ0=sQuery(id+"F0.wireOp",EDGE,"E5.bottom");var subQ1=sQuery(id+"F0.wireOp",EDGE,"E1.bottom");var subQ2=makeQuery(id+"F0.imprint","INTERSECT",VERTEX,{"derivedFrom":[subQ1,subQ0]});Q102=makeQuery(id+"F0.imprint","IMPRINT",FACE,{"disambiguationData":[TD([[makeQuery(id+"F0.imprint","IMPRINT",EDGE,{"disambiguationData":[TD([[subQ2,-1.0]])],"derivedFrom":subQ1}),1.0]])]});}
            var Q103;
            {var subQ0=sQuery(id+"F0.wireOp",EDGE,"E8.top");var subQ1=sQuery(id+"F0.wireOp",EDGE,"E2.top");var subQ2=makeQuery(id+"F0.imprint","INTERSECT",VERTEX,{"derivedFrom":[subQ1,subQ0]});Q103=makeQuery(id+"F0.imprint","IMPRINT",FACE,{"disambiguationData":[TD([[makeQuery(id+"F0.imprint","IMPRINT",EDGE,{"disambiguationData":[TD([[subQ2,-1.0]])],"derivedFrom":subQ1}),-1.0]])]});}
            var Q104;
            {var subQ0=sQuery(id+"F0.wireOp",EDGE,"E8.bottom");var subQ1=sQuery(id+"F0.wireOp",EDGE,"E4.bottom");var subQ2=makeQuery(id+"F0.imprint","INTERSECT",VERTEX,{"derivedFrom":[subQ1,subQ0]});Q104=makeQuery(id+"F0.imprint","IMPRINT",FACE,{"disambiguationData":[TD([[makeQuery(id+"F0.imprint","IMPRINT",EDGE,{"disambiguationData":[TD([[subQ2,-1.0]])],"derivedFrom":subQ1}),1.0]])]});}
            var Q105;
            {var subQ0=sQuery(id+"F0.wireOp",EDGE,"E3.top");var subQ1=sQuery(id+"F0.wireOp",EDGE,"E2.top");var subQ2=makeQuery(id+"F0.imprint","INTERSECT",VERTEX,{"derivedFrom":[subQ1,subQ0]});Q105=makeQuery(id+"F0.imprint","IMPRINT",FACE,{"disambiguationData":[TD([[makeQuery(id+"F0.imprint","IMPRINT",EDGE,{"disambiguationData":[TD([[subQ2,-1.0]])],"derivedFrom":subQ1}),-1.0]])]});}
            var Q106;
            {var subQ0=sQuery(id+"F0.wireOp",EDGE,"E4.top");var subQ1=sQuery(id+"F0.wireOp",EDGE,"E2.top");var subQ2=makeQuery(id+"F0.imprint","INTERSECT",VERTEX,{"derivedFrom":[subQ1,subQ0]});Q106=makeQuery(id+"F0.imprint","IMPRINT",FACE,{"disambiguationData":[TD([[makeQuery(id+"F0.imprint","IMPRINT",EDGE,{"disambiguationData":[TD([[subQ2,-1.0]])],"derivedFrom":subQ1}),1.0]])]});}
            var Q107;
            {var subQ0=sQuery(id+"F0.wireOp",EDGE,"E3.top");var subQ1=sQuery(id+"F0.wireOp",EDGE,"E1.top");var subQ2=makeQuery(id+"F0.imprint","INTERSECT",VERTEX,{"derivedFrom":[subQ1,subQ0]});Q107=makeQuery(id+"F0.imprint","IMPRINT",FACE,{"disambiguationData":[TD([[makeQuery(id+"F0.imprint","IMPRINT",EDGE,{"disambiguationData":[TD([[subQ2,-1.0]])],"derivedFrom":subQ1}),1.0]])]});}
            var Q108;
            {var subQ0=sQuery(id+"F0.wireOp",EDGE,"E3.bottom");var subQ1=sQuery(id+"F0.wireOp",EDGE,"E1.bottom");var subQ2=makeQuery(id+"F0.imprint","INTERSECT",VERTEX,{"derivedFrom":[subQ1,subQ0]});Q108=makeQuery(id+"F0.imprint","IMPRINT",FACE,{"disambiguationData":[TD([[makeQuery(id+"F0.imprint","IMPRINT",EDGE,{"disambiguationData":[TD([[subQ2,-1.0]])],"derivedFrom":subQ1}),-1.0]])]});}
            var Q109;
            {var subQ0=sQuery(id+"F0.wireOp",EDGE,"E8.bottom");var subQ1=sQuery(id+"F0.wireOp",EDGE,"E6.bottom");var subQ2=makeQuery(id+"F0.imprint","INTERSECT",VERTEX,{"derivedFrom":[subQ1,subQ0]});Q109=makeQuery(id+"F0.imprint","IMPRINT",FACE,{"disambiguationData":[TD([[makeQuery(id+"F0.imprint","IMPRINT",EDGE,{"disambiguationData":[TD([[subQ2,-1.0]])],"derivedFrom":subQ1}),-1.0]])]});}
            var Q110;
            {var subQ0=sQuery(id+"F0.wireOp",EDGE,"E5.bottom");var subQ1=sQuery(id+"F0.wireOp",EDGE,"E3.bottom");var subQ2=makeQuery(id+"F0.imprint","INTERSECT",VERTEX,{"derivedFrom":[subQ1,subQ0]});Q110=makeQuery(id+"F0.imprint","IMPRINT",FACE,{"disambiguationData":[TD([[makeQuery(id+"F0.imprint","IMPRINT",EDGE,{"disambiguationData":[TD([[subQ2,-1.0]])],"derivedFrom":subQ1}),-1.0]])]});}
            var Q111;
            {var subQ0=sQuery(id+"F0.wireOp",EDGE,"E2.bottom");var subQ1=sQuery(id+"F0.wireOp",EDGE,"E1.bottom");var subQ2=makeQuery(id+"F0.imprint","INTERSECT",VERTEX,{"derivedFrom":[subQ1,subQ0]});Q111=makeQuery(id+"F0.imprint","IMPRINT",FACE,{"disambiguationData":[TD([[makeQuery(id+"F0.imprint","IMPRINT",EDGE,{"disambiguationData":[TD([[subQ2,-1.0]])],"derivedFrom":subQ1}),-1.0]])]});}
            var Q112;
            {var subQ0=sQuery(id+"F0.wireOp",EDGE,"E7.top");var subQ1=sQuery(id+"F0.wireOp",EDGE,"E1.bottom");var subQ2=makeQuery(id+"F0.imprint","INTERSECT",VERTEX,{"derivedFrom":[subQ1,subQ0]});Q112=makeQuery(id+"F0.imprint","IMPRINT",FACE,{"disambiguationData":[TD([[makeQuery(id+"F0.imprint","IMPRINT",EDGE,{"disambiguationData":[TD([[subQ2,-1.0]])],"derivedFrom":subQ1}),-1.0]])]});}
            var Q113;
            {var subQ5=sQuery(id+"F0.wireOp",EDGE,"E6.top");var subQ6=sQuery(id+"F0.wireOp",EDGE,"E1.bottom");var subQ7=makeQuery(id+"F0.imprint","INTERSECT",VERTEX,{"derivedFrom":[subQ6,subQ5]});Q113=makeQuery(id+"F0.imprint","IMPRINT",FACE,{"disambiguationData":[TD([[makeQuery(id+"F0.imprint","IMPRINT",EDGE,{"disambiguationData":[TD([[subQ7,-1.0]])],"derivedFrom":subQ6}),-1.0]])]});}
            var Q114;
            {var subQ0=sQuery(id+"F0.wireOp",EDGE,"E7.bottom");var subQ1=sQuery(id+"F0.wireOp",EDGE,"E2.bottom");var subQ2=makeQuery(id+"F0.imprint","INTERSECT",VERTEX,{"derivedFrom":[subQ1,subQ0]});Q114=makeQuery(id+"F0.imprint","IMPRINT",FACE,{"disambiguationData":[TD([[makeQuery(id+"F0.imprint","IMPRINT",EDGE,{"disambiguationData":[TD([[subQ2,-1.0]])],"derivedFrom":subQ1}),-1.0]])]});}
            var Q115;
            {var subQ0=sQuery(id+"F0.wireOp",EDGE,"E7.bottom");var subQ1=sQuery(id+"F0.wireOp",EDGE,"E3.bottom");var subQ2=makeQuery(id+"F0.imprint","INTERSECT",VERTEX,{"derivedFrom":[subQ1,subQ0]});Q115=makeQuery(id+"F0.imprint","IMPRINT",FACE,{"disambiguationData":[TD([[makeQuery(id+"F0.imprint","IMPRINT",EDGE,{"disambiguationData":[TD([[subQ2,-1.0]])],"derivedFrom":subQ1}),1.0]])]});}
            var Q116;
            {var subQ0=sQuery(id+"F0.wireOp",EDGE,"E6.top");var subQ1=sQuery(id+"F0.wireOp",EDGE,"E2.top");var subQ2=makeQuery(id+"F0.imprint","INTERSECT",VERTEX,{"derivedFrom":[subQ1,subQ0]});Q116=makeQuery(id+"F0.imprint","IMPRINT",FACE,{"disambiguationData":[TD([[makeQuery(id+"F0.imprint","IMPRINT",EDGE,{"disambiguationData":[TD([[subQ2,-1.0]])],"derivedFrom":subQ1}),-1.0]])]});}
            var Q117;
            {var subQ0=sQuery(id+"F0.wireOp",EDGE,"E8.top");var subQ1=sQuery(id+"F0.wireOp",EDGE,"E1.top");var subQ2=makeQuery(id+"F0.imprint","INTERSECT",VERTEX,{"derivedFrom":[subQ1,subQ0]});Q117=makeQuery(id+"F0.imprint","IMPRINT",FACE,{"disambiguationData":[TD([[makeQuery(id+"F0.imprint","IMPRINT",EDGE,{"disambiguationData":[TD([[subQ2,-1.0]])],"derivedFrom":subQ1}),1.0]])]});}
            var Q118;
            {var subQ0=sQuery(id+"F0.wireOp",EDGE,"E8.bottom");var subQ1=sQuery(id+"F0.wireOp",EDGE,"E2.bottom");var subQ2=makeQuery(id+"F0.imprint","INTERSECT",VERTEX,{"derivedFrom":[subQ1,subQ0]});Q118=makeQuery(id+"F0.imprint","IMPRINT",FACE,{"disambiguationData":[TD([[makeQuery(id+"F0.imprint","IMPRINT",EDGE,{"disambiguationData":[TD([[subQ2,-1.0]])],"derivedFrom":subQ1}),-1.0]])]});}
            var Q119;
            {var subQ0=sQuery(id+"F0.wireOp",EDGE,"E4.top");var subQ1=sQuery(id+"F0.wireOp",EDGE,"E3.top");var subQ2=makeQuery(id+"F0.imprint","INTERSECT",VERTEX,{"derivedFrom":[subQ1,subQ0]});Q119=makeQuery(id+"F0.imprint","IMPRINT",FACE,{"disambiguationData":[TD([[makeQuery(id+"F0.imprint","IMPRINT",EDGE,{"disambiguationData":[TD([[subQ2,-1.0]])],"derivedFrom":subQ1}),1.0]])]});}
            var Q120;
            {var subQ0=sQuery(id+"F0.wireOp",EDGE,"E3.top");var subQ1=sQuery(id+"F0.wireOp",EDGE,"E2.top");var subQ2=makeQuery(id+"F0.imprint","INTERSECT",VERTEX,{"derivedFrom":[subQ1,subQ0]});Q120=makeQuery(id+"F0.imprint","IMPRINT",FACE,{"disambiguationData":[TD([[makeQuery(id+"F0.imprint","IMPRINT",EDGE,{"disambiguationData":[TD([[subQ2,-1.0]])],"derivedFrom":subQ1}),1.0]])]});}
            var Q121;
            {var subQ0=sQuery(id+"F0.wireOp",EDGE,"E5.bottom");var subQ1=sQuery(id+"F0.wireOp",EDGE,"E2.bottom");var subQ2=makeQuery(id+"F0.imprint","INTERSECT",VERTEX,{"derivedFrom":[subQ1,subQ0]});Q121=makeQuery(id+"F0.imprint","IMPRINT",FACE,{"disambiguationData":[TD([[makeQuery(id+"F0.imprint","IMPRINT",EDGE,{"disambiguationData":[TD([[subQ2,-1.0]])],"derivedFrom":subQ1}),-1.0]])]});}
            var Q122;
            {var subQ0=sQuery(id+"F0.wireOp",EDGE,"E4.bottom");var subQ1=sQuery(id+"F0.wireOp",EDGE,"E1.bottom");var subQ2=makeQuery(id+"F0.imprint","INTERSECT",VERTEX,{"derivedFrom":[subQ1,subQ0]});Q122=makeQuery(id+"F0.imprint","IMPRINT",FACE,{"disambiguationData":[TD([[makeQuery(id+"F0.imprint","IMPRINT",EDGE,{"disambiguationData":[TD([[subQ2,-1.0]])],"derivedFrom":subQ1}),-1.0]])]});}
            var Q123;
            {var subQ0=sQuery(id+"F0.wireOp",EDGE,"E4.top");var subQ1=sQuery(id+"F0.wireOp",EDGE,"E2.top");var subQ2=makeQuery(id+"F0.imprint","INTERSECT",VERTEX,{"derivedFrom":[subQ1,subQ0]});Q123=makeQuery(id+"F0.imprint","IMPRINT",FACE,{"disambiguationData":[TD([[makeQuery(id+"F0.imprint","IMPRINT",EDGE,{"disambiguationData":[TD([[subQ2,-1.0]])],"derivedFrom":subQ1}),-1.0]])]});}
            var Q124;
            {var subQ0=sQuery(id+"F0.wireOp",EDGE,"E5.bottom");var subQ1=sQuery(id+"F0.wireOp",EDGE,"E2.bottom");var subQ2=makeQuery(id+"F0.imprint","INTERSECT",VERTEX,{"derivedFrom":[subQ1,subQ0]});Q124=makeQuery(id+"F0.imprint","IMPRINT",FACE,{"disambiguationData":[TD([[makeQuery(id+"F0.imprint","IMPRINT",EDGE,{"disambiguationData":[TD([[subQ2,-1.0]])],"derivedFrom":subQ1}),1.0]])]});}
            var Q125;
            {var subQ0=sQuery(id+"F0.wireOp",EDGE,"E7.bottom");var subQ1=sQuery(id+"F0.wireOp",EDGE,"E1.top");var subQ2=makeQuery(id+"F0.imprint","INTERSECT",VERTEX,{"derivedFrom":[subQ1,subQ0]});Q125=makeQuery(id+"F0.imprint","IMPRINT",FACE,{"disambiguationData":[TD([[makeQuery(id+"F0.imprint","IMPRINT",EDGE,{"disambiguationData":[TD([[subQ2,-1.0]])],"derivedFrom":subQ1}),1.0]])]});}
            var Q126;
            {var subQ0=sQuery(id+"F0.wireOp",EDGE,"E6.top");var subQ1=sQuery(id+"F0.wireOp",EDGE,"E1.bottom");var subQ2=makeQuery(id+"F0.imprint","INTERSECT",VERTEX,{"derivedFrom":[subQ1,subQ0]});Q126=makeQuery(id+"F0.imprint","IMPRINT",FACE,{"disambiguationData":[TD([[makeQuery(id+"F0.imprint","IMPRINT",EDGE,{"disambiguationData":[TD([[subQ2,-1.0]])],"derivedFrom":subQ1}),1.0]])]});}
            var Q127;
            {var subQ0=sQuery(id+"F0.wireOp",EDGE,"E8.bottom");var subQ1=sQuery(id+"F0.wireOp",EDGE,"E3.bottom");var subQ2=makeQuery(id+"F0.imprint","INTERSECT",VERTEX,{"derivedFrom":[subQ1,subQ0]});Q127=makeQuery(id+"F0.imprint","IMPRINT",FACE,{"disambiguationData":[TD([[makeQuery(id+"F0.imprint","IMPRINT",EDGE,{"disambiguationData":[TD([[subQ2,-1.0]])],"derivedFrom":subQ1}),1.0]])]});}
            var Q128;
            {var subQ0=sQuery(id+"F0.wireOp",EDGE,"E4.top");var subQ1=sQuery(id+"F0.wireOp",EDGE,"E1.top");var subQ2=makeQuery(id+"F0.imprint","INTERSECT",VERTEX,{"derivedFrom":[subQ1,subQ0]});Q128=makeQuery(id+"F0.imprint","IMPRINT",FACE,{"disambiguationData":[TD([[makeQuery(id+"F0.imprint","IMPRINT",EDGE,{"disambiguationData":[TD([[subQ2,-1.0]])],"derivedFrom":subQ1}),1.0]])]});}
            var Q129;
            {var subQ0=sQuery(id+"F0.wireOp",EDGE,"E5.top");var subQ1=sQuery(id+"F0.wireOp",EDGE,"E1.top");var subQ2=makeQuery(id+"F0.imprint","INTERSECT",VERTEX,{"derivedFrom":[subQ1,subQ0]});Q129=makeQuery(id+"F0.imprint","IMPRINT",FACE,{"disambiguationData":[TD([[makeQuery(id+"F0.imprint","IMPRINT",EDGE,{"disambiguationData":[TD([[subQ2,-1.0]])],"derivedFrom":subQ1}),-1.0]])]});}
            var Q130;
            {var subQ0=sQuery(id+"F0.wireOp",EDGE,"E7.top");var subQ1=sQuery(id+"F0.wireOp",EDGE,"E3.top");var subQ2=makeQuery(id+"F0.imprint","INTERSECT",VERTEX,{"derivedFrom":[subQ1,subQ0]});Q130=makeQuery(id+"F0.imprint","IMPRINT",FACE,{"disambiguationData":[TD([[makeQuery(id+"F0.imprint","IMPRINT",EDGE,{"disambiguationData":[TD([[subQ2,-1.0]])],"derivedFrom":subQ1}),-1.0]])]});}
            var Q131;
            {var subQ0=sQuery(id+"F0.wireOp",EDGE,"E8.top");var subQ1=sQuery(id+"F0.wireOp",EDGE,"E1.bottom");var subQ2=makeQuery(id+"F0.imprint","INTERSECT",VERTEX,{"derivedFrom":[subQ1,subQ0]});Q131=makeQuery(id+"F0.imprint","IMPRINT",FACE,{"disambiguationData":[TD([[makeQuery(id+"F0.imprint","IMPRINT",EDGE,{"disambiguationData":[TD([[subQ2,-1.0]])],"derivedFrom":subQ1}),-1.0]])]});}
            var Q132;
            {var subQ0=sQuery(id+"F0.wireOp",EDGE,"E6.top");var subQ1=sQuery(id+"F0.wireOp",EDGE,"E2.top");var subQ2=makeQuery(id+"F0.imprint","INTERSECT",VERTEX,{"derivedFrom":[subQ1,subQ0]});Q132=makeQuery(id+"F0.imprint","IMPRINT",FACE,{"disambiguationData":[TD([[makeQuery(id+"F0.imprint","IMPRINT",EDGE,{"disambiguationData":[TD([[subQ2,-1.0]])],"derivedFrom":subQ1}),1.0]])]});}
            var Q133;
            {var subQ0=sQuery(id+"F0.wireOp",EDGE,"E7.top");var subQ1=sQuery(id+"F0.wireOp",EDGE,"E2.top");var subQ2=makeQuery(id+"F0.imprint","INTERSECT",VERTEX,{"derivedFrom":[subQ1,subQ0]});Q133=makeQuery(id+"F0.imprint","IMPRINT",FACE,{"disambiguationData":[TD([[makeQuery(id+"F0.imprint","IMPRINT",EDGE,{"disambiguationData":[TD([[subQ2,-1.0]])],"derivedFrom":subQ1}),1.0]])]});}
            var Q134;
            {var subQ0=sQuery(id+"F0.wireOp",EDGE,"E7.bottom");var subQ1=sQuery(id+"F0.wireOp",EDGE,"E2.bottom");var subQ2=makeQuery(id+"F0.imprint","INTERSECT",VERTEX,{"derivedFrom":[subQ1,subQ0]});Q134=makeQuery(id+"F0.imprint","IMPRINT",FACE,{"disambiguationData":[TD([[makeQuery(id+"F0.imprint","IMPRINT",EDGE,{"disambiguationData":[TD([[subQ2,-1.0]])],"derivedFrom":subQ1}),1.0]])]});}
            var Q135;
            {var subQ0=sQuery(id+"F0.wireOp",EDGE,"E2.top");var subQ1=sQuery(id+"F0.wireOp",EDGE,"E1.top");var subQ2=makeQuery(id+"F0.imprint","INTERSECT",VERTEX,{"derivedFrom":[subQ1,subQ0]});Q135=makeQuery(id+"F0.imprint","IMPRINT",FACE,{"disambiguationData":[TD([[makeQuery(id+"F0.imprint","IMPRINT",EDGE,{"disambiguationData":[TD([[subQ2,-1.0]])],"derivedFrom":subQ1}),1.0]])]});}
            var Q136;
            {var subQ0=sQuery(id+"F0.wireOp",EDGE,"E4.bottom");var subQ1=sQuery(id+"F0.wireOp",EDGE,"E2.bottom");var subQ2=makeQuery(id+"F0.imprint","INTERSECT",VERTEX,{"derivedFrom":[subQ1,subQ0]});Q136=makeQuery(id+"F0.imprint","IMPRINT",FACE,{"disambiguationData":[TD([[makeQuery(id+"F0.imprint","IMPRINT",EDGE,{"disambiguationData":[TD([[subQ2,-1.0]])],"derivedFrom":subQ1}),1.0]])]});}
            var Q137;
            {var subQ0=sQuery(id+"F0.wireOp",EDGE,"E8.bottom");var subQ1=sQuery(id+"F0.wireOp",EDGE,"E2.bottom");var subQ2=makeQuery(id+"F0.imprint","INTERSECT",VERTEX,{"derivedFrom":[subQ1,subQ0]});Q137=makeQuery(id+"F0.imprint","IMPRINT",FACE,{"disambiguationData":[TD([[makeQuery(id+"F0.imprint","IMPRINT",EDGE,{"disambiguationData":[TD([[subQ2,-1.0]])],"derivedFrom":subQ1}),1.0]])]});}
            var Q138;
            {var subQ0=sQuery(id+"F0.wireOp",EDGE,"E5.bottom");var subQ1=sQuery(id+"F0.wireOp",EDGE,"E1.bottom");var subQ2=makeQuery(id+"F0.imprint","INTERSECT",VERTEX,{"derivedFrom":[subQ1,subQ0]});Q138=makeQuery(id+"F0.imprint","IMPRINT",FACE,{"disambiguationData":[TD([[makeQuery(id+"F0.imprint","IMPRINT",EDGE,{"disambiguationData":[TD([[subQ2,-1.0]])],"derivedFrom":subQ1}),-1.0]])]});}
            var Q139;
            {var subQ0=sQuery(id+"F0.wireOp",EDGE,"E6.bottom");var subQ1=sQuery(id+"F0.wireOp",EDGE,"E1.top");var subQ2=makeQuery(id+"F0.imprint","INTERSECT",VERTEX,{"derivedFrom":[subQ1,subQ0]});Q139=makeQuery(id+"F0.imprint","IMPRINT",FACE,{"disambiguationData":[TD([[makeQuery(id+"F0.imprint","IMPRINT",EDGE,{"disambiguationData":[TD([[subQ2,-1.0]])],"derivedFrom":subQ1}),1.0]])]});}
            var Q140;
            {var subQ0=sQuery(id+"F0.wireOp",EDGE,"E4.bottom");var subQ1=sQuery(id+"F0.wireOp",EDGE,"E2.bottom");var subQ2=makeQuery(id+"F0.imprint","INTERSECT",VERTEX,{"derivedFrom":[subQ1,subQ0]});Q140=makeQuery(id+"F0.imprint","IMPRINT",FACE,{"disambiguationData":[TD([[makeQuery(id+"F0.imprint","IMPRINT",EDGE,{"disambiguationData":[TD([[subQ2,-1.0]])],"derivedFrom":subQ1}),-1.0]])]});}
            var Q141;
            {var subQ0=sQuery(id+"F0.wireOp",EDGE,"E7.top");var subQ1=sQuery(id+"F0.wireOp",EDGE,"E2.top");var subQ2=makeQuery(id+"F0.imprint","INTERSECT",VERTEX,{"derivedFrom":[subQ1,subQ0]});Q141=makeQuery(id+"F0.imprint","IMPRINT",FACE,{"disambiguationData":[TD([[makeQuery(id+"F0.imprint","IMPRINT",EDGE,{"disambiguationData":[TD([[subQ2,-1.0]])],"derivedFrom":subQ1}),-1.0]])]});}
            var Q142;
            {var subQ0=sQuery(id+"F0.wireOp",EDGE,"E7.top");var subQ1=sQuery(id+"F0.wireOp",EDGE,"E6.top");var subQ2=makeQuery(id+"F0.imprint","INTERSECT",VERTEX,{"derivedFrom":[subQ1,subQ0]});Q142=makeQuery(id+"F0.imprint","IMPRINT",FACE,{"disambiguationData":[TD([[makeQuery(id+"F0.imprint","IMPRINT",EDGE,{"disambiguationData":[TD([[subQ2,-1.0]])],"derivedFrom":subQ1}),1.0]])]});}
            var Q143;
            {var subQ0=sQuery(id+"F0.wireOp",EDGE,"E2.top");var subQ1=sQuery(id+"F0.wireOp",EDGE,"E1.bottom");var subQ2=makeQuery(id+"F0.imprint","INTERSECT",VERTEX,{"derivedFrom":[subQ1,subQ0]});Q143=makeQuery(id+"F0.imprint","IMPRINT",FACE,{"disambiguationData":[TD([[makeQuery(id+"F0.imprint","IMPRINT",EDGE,{"disambiguationData":[TD([[subQ2,-1.0]])],"derivedFrom":subQ1}),-1.0]])]});}
            var Q144;
            {var subQ0=sQuery(id+"F0.wireOp",EDGE,"E3.bottom");var subQ1=sQuery(id+"F0.wireOp",EDGE,"E2.bottom");var subQ2=makeQuery(id+"F0.imprint","INTERSECT",VERTEX,{"derivedFrom":[subQ1,subQ0]});Q144=makeQuery(id+"F0.imprint","IMPRINT",FACE,{"disambiguationData":[TD([[makeQuery(id+"F0.imprint","IMPRINT",EDGE,{"disambiguationData":[TD([[subQ2,-1.0]])],"derivedFrom":subQ1}),1.0]])]});}
            extrude(context, id + "F2", {"entities" : qUnion([Q0, Q1, Q2, Q3, Q4, Q5, Q6, Q7, Q8, Q9, Q10, Q11, Q12, Q13, Q14, Q15, Q16, Q17, Q18, Q19, Q20, Q21, Q22, Q23, Q24, Q25, Q26, Q27, Q28, Q29, Q30, Q31, Q32, Q33, Q34, Q35, Q36, Q37, Q38, Q39, Q40, Q41, Q42, Q43, Q44, Q45, Q46, Q47, Q48, Q49, Q50, Q51, Q52, Q53, Q54, Q55, Q56, Q57, Q58, Q59, Q60, Q61, Q62, Q63, Q64, Q65, Q66, Q67, Q68, Q69, Q70, Q71, Q72, Q73, Q74, Q75, Q76, Q77, Q78, Q79, Q80, Q81, Q82, Q83, Q84, Q85, Q86, Q87, Q88, Q89, Q90, Q91, Q92, Q93, Q94, Q95, Q96, Q97, Q98, Q99, Q100, Q101, Q102, Q103, Q104, Q105, Q106, Q107, Q108, Q109, Q110, Q111, Q112, Q113, Q114, Q115, Q116, Q117, Q118, Q119, Q120, Q121, Q122, Q123, Q124, Q125, Q126, Q127, Q128, Q129, Q130, Q131, Q132, Q133, Q134, Q135, Q136, Q137, Q138, Q139, Q140, Q141, Q142, Q143, Q144]), "depth" : 25.4 * mm});
        }
        {
            var Q0;
            Q0=makeQuery(id+"F2.opExtrude","SWEPT_BODY",BODY,{"disambiguationData":[OSD([sQuery(id+"F0.wireOp",EDGE,"E0"),sQuery(id+"F0.wireOp",EDGE,"E1.bottom"),sQuery(id+"F0.wireOp",EDGE,"E1.top"),sQuery(id+"F0.wireOp",EDGE,"E1.left"),sQuery(id+"F0.wireOp",EDGE,"E1.right"),sQuery(id+"F0.wireOp",EDGE,"E2.bottom"),sQuery(id+"F0.wireOp",EDGE,"E2.top"),sQuery(id+"F0.wireOp",EDGE,"E2.left"),sQuery(id+"F0.wireOp",EDGE,"E2.right"),sQuery(id+"F0.wireOp",EDGE,"E3.bottom"),sQuery(id+"F0.wireOp",EDGE,"E3.top"),sQuery(id+"F0.wireOp",EDGE,"E3.left"),sQuery(id+"F0.wireOp",EDGE,"E3.right"),sQuery(id+"F0.wireOp",EDGE,"E4.bottom"),sQuery(id+"F0.wireOp",EDGE,"E4.top"),sQuery(id+"F0.wireOp",EDGE,"E4.left"),sQuery(id+"F0.wireOp",EDGE,"E4.right"),sQuery(id+"F0.wireOp",EDGE,"E5.bottom"),sQuery(id+"F0.wireOp",EDGE,"E5.top"),sQuery(id+"F0.wireOp",EDGE,"E5.left"),sQuery(id+"F0.wireOp",EDGE,"E5.right"),sQuery(id+"F0.wireOp",EDGE,"E6.bottom"),sQuery(id+"F0.wireOp",EDGE,"E6.top"),sQuery(id+"F0.wireOp",EDGE,"E6.left"),sQuery(id+"F0.wireOp",EDGE,"E6.right"),sQuery(id+"F0.wireOp",EDGE,"E7.bottom"),sQuery(id+"F0.wireOp",EDGE,"E7.top"),sQuery(id+"F0.wireOp",EDGE,"E7.left"),sQuery(id+"F0.wireOp",EDGE,"E7.right"),sQuery(id+"F0.wireOp",EDGE,"E8.bottom"),sQuery(id+"F0.wireOp",EDGE,"E8.top"),sQuery(id+"F0.wireOp",EDGE,"E8.left"),sQuery(id+"F0.wireOp",EDGE,"E8.right")])]});
            var Q1;
            Q1=sQuery(id+"F0.wireOp",VERTEX,"E0.center");
            transform(context, id + "F3", {"entities" : qUnion([Q0]), "transformType" : TransformType.SCALE_UNIFORMLY, "scale" : .5, "scalePoint" : qUnion([Q1]), "makeCopy" : true});
        }
        {
            var Q0;
            Q0=makeQuery(id+"F3.opPattern","COPY",BODY,{"derivedFrom":makeQuery(id+"F2.opExtrude","SWEPT_BODY",BODY,{"disambiguationData":[OSD([sQuery(id+"F0.wireOp",EDGE,"E0"),sQuery(id+"F0.wireOp",EDGE,"E1.bottom"),sQuery(id+"F0.wireOp",EDGE,"E1.top"),sQuery(id+"F0.wireOp",EDGE,"E1.left"),sQuery(id+"F0.wireOp",EDGE,"E1.right"),sQuery(id+"F0.wireOp",EDGE,"E2.bottom"),sQuery(id+"F0.wireOp",EDGE,"E2.top"),sQuery(id+"F0.wireOp",EDGE,"E2.left"),sQuery(id+"F0.wireOp",EDGE,"E2.right"),sQuery(id+"F0.wireOp",EDGE,"E3.bottom"),sQuery(id+"F0.wireOp",EDGE,"E3.top"),sQuery(id+"F0.wireOp",EDGE,"E3.left"),sQuery(id+"F0.wireOp",EDGE,"E3.right"),sQuery(id+"F0.wireOp",EDGE,"E4.bottom"),sQuery(id+"F0.wireOp",EDGE,"E4.top"),sQuery(id+"F0.wireOp",EDGE,"E4.left"),sQuery(id+"F0.wireOp",EDGE,"E4.right"),sQuery(id+"F0.wireOp",EDGE,"E5.bottom"),sQuery(id+"F0.wireOp",EDGE,"E5.top"),sQuery(id+"F0.wireOp",EDGE,"E5.left"),sQuery(id+"F0.wireOp",EDGE,"E5.right"),sQuery(id+"F0.wireOp",EDGE,"E6.bottom"),sQuery(id+"F0.wireOp",EDGE,"E6.top"),sQuery(id+"F0.wireOp",EDGE,"E6.left"),sQuery(id+"F0.wireOp",EDGE,"E6.right"),sQuery(id+"F0.wireOp",EDGE,"E7.bottom"),sQuery(id+"F0.wireOp",EDGE,"E7.top"),sQuery(id+"F0.wireOp",EDGE,"E7.left"),sQuery(id+"F0.wireOp",EDGE,"E7.right"),sQuery(id+"F0.wireOp",EDGE,"E8.bottom"),sQuery(id+"F0.wireOp",EDGE,"E8.top"),sQuery(id+"F0.wireOp",EDGE,"E8.left"),sQuery(id+"F0.wireOp",EDGE,"E8.right")])]}),"instanceName":"1"});
            var Q1;
            Q1=qCreatedBy(makeId("Front.planeOp"),FACE);
            transform(context, id + "F4", {"entities" : qUnion([Q0]), "transformType" : TransformType.TRANSLATION_DISTANCE, "transformDirection" : qUnion([Q1]), "distance" : 50.8 * mm, "makeCopy" : false});
        }
        {
            var Q0;
            Q0=makeQuery(id+"F3.opPattern","COPY",FACE,{"derivedFrom":makeQuery(id+"F2.opExtrude","CAP_FACE",FACE,{"disambiguationData":[OSD([sQuery(id+"F0.wireOp",EDGE,"E0"),sQuery(id+"F0.wireOp",EDGE,"E1.bottom"),sQuery(id+"F0.wireOp",EDGE,"E1.top"),sQuery(id+"F0.wireOp",EDGE,"E1.left"),sQuery(id+"F0.wireOp",EDGE,"E1.right"),sQuery(id+"F0.wireOp",EDGE,"E2.bottom"),sQuery(id+"F0.wireOp",EDGE,"E2.top"),sQuery(id+"F0.wireOp",EDGE,"E2.left"),sQuery(id+"F0.wireOp",EDGE,"E2.right"),sQuery(id+"F0.wireOp",EDGE,"E3.bottom"),sQuery(id+"F0.wireOp",EDGE,"E3.top"),sQuery(id+"F0.wireOp",EDGE,"E3.left"),sQuery(id+"F0.wireOp",EDGE,"E3.right"),sQuery(id+"F0.wireOp",EDGE,"E4.bottom"),sQuery(id+"F0.wireOp",EDGE,"E4.top"),sQuery(id+"F0.wireOp",EDGE,"E4.left"),sQuery(id+"F0.wireOp",EDGE,"E4.right"),sQuery(id+"F0.wireOp",EDGE,"E5.bottom"),sQuery(id+"F0.wireOp",EDGE,"E5.top"),sQuery(id+"F0.wireOp",EDGE,"E5.left"),sQuery(id+"F0.wireOp",EDGE,"E5.right"),sQuery(id+"F0.wireOp",EDGE,"E6.bottom"),sQuery(id+"F0.wireOp",EDGE,"E6.top"),sQuery(id+"F0.wireOp",EDGE,"E6.left"),sQuery(id+"F0.wireOp",EDGE,"E6.right"),sQuery(id+"F0.wireOp",EDGE,"E7.bottom"),sQuery(id+"F0.wireOp",EDGE,"E7.top"),sQuery(id+"F0.wireOp",EDGE,"E7.left"),sQuery(id+"F0.wireOp",EDGE,"E7.right"),sQuery(id+"F0.wireOp",EDGE,"E8.bottom"),sQuery(id+"F0.wireOp",EDGE,"E8.top"),sQuery(id+"F0.wireOp",EDGE,"E8.left"),sQuery(id+"F0.wireOp",EDGE,"E8.right")])],"isStart":false}),"instanceName":"1"});
            var Q1;
            Q1=makeQuery(id+"F2.opExtrude","CAP_FACE",FACE,{"disambiguationData":[OSD([sQuery(id+"F0.wireOp",EDGE,"E0"),sQuery(id+"F0.wireOp",EDGE,"E1.bottom"),sQuery(id+"F0.wireOp",EDGE,"E1.top"),sQuery(id+"F0.wireOp",EDGE,"E1.left"),sQuery(id+"F0.wireOp",EDGE,"E1.right"),sQuery(id+"F0.wireOp",EDGE,"E2.bottom"),sQuery(id+"F0.wireOp",EDGE,"E2.top"),sQuery(id+"F0.wireOp",EDGE,"E2.left"),sQuery(id+"F0.wireOp",EDGE,"E2.right"),sQuery(id+"F0.wireOp",EDGE,"E3.bottom"),sQuery(id+"F0.wireOp",EDGE,"E3.top"),sQuery(id+"F0.wireOp",EDGE,"E3.left"),sQuery(id+"F0.wireOp",EDGE,"E3.right"),sQuery(id+"F0.wireOp",EDGE,"E4.bottom"),sQuery(id+"F0.wireOp",EDGE,"E4.top"),sQuery(id+"F0.wireOp",EDGE,"E4.left"),sQuery(id+"F0.wireOp",EDGE,"E4.right"),sQuery(id+"F0.wireOp",EDGE,"E5.bottom"),sQuery(id+"F0.wireOp",EDGE,"E5.top"),sQuery(id+"F0.wireOp",EDGE,"E5.left"),sQuery(id+"F0.wireOp",EDGE,"E5.right"),sQuery(id+"F0.wireOp",EDGE,"E6.bottom"),sQuery(id+"F0.wireOp",EDGE,"E6.top"),sQuery(id+"F0.wireOp",EDGE,"E6.left"),sQuery(id+"F0.wireOp",EDGE,"E6.right"),sQuery(id+"F0.wireOp",EDGE,"E7.bottom"),sQuery(id+"F0.wireOp",EDGE,"E7.top"),sQuery(id+"F0.wireOp",EDGE,"E7.left"),sQuery(id+"F0.wireOp",EDGE,"E7.right"),sQuery(id+"F0.wireOp",EDGE,"E8.bottom"),sQuery(id+"F0.wireOp",EDGE,"E8.top"),sQuery(id+"F0.wireOp",EDGE,"E8.left"),sQuery(id+"F0.wireOp",EDGE,"E8.right")])],"isStart":false});
            loft(context, id + "F5", {"sheetProfilesArray" : [{ "sheetProfileEntities" : qUnion([Q0]) }, { "sheetProfileEntities" : qUnion([Q1]) }]});
        }
        {
            var Q0;
            Q0 = qSketchRegion(id + "F0", true);
            var Q1;
            Q1=sQuery(id+"F0.wireOp",EDGE,"E7.bottom");
            var Q2;
            Q2=sQuery(id+"F0.wireOp",EDGE,"E8.bottom");
            var Q3;
            Q3=sQuery(id+"F0.wireOp",EDGE,"E2.bottom");
            var Q4;
            Q4=sQuery(id+"F0.wireOp",EDGE,"E5.top");
            var Q5;
            Q5=sQuery(id+"F0.wireOp",EDGE,"E5.bottom");
            var Q6;
            Q6=sQuery(id+"F0.wireOp",EDGE,"E0");
            var Q7;
            Q7=sQuery(id+"F0.wireOp",EDGE,"E6.bottom");
            var Q8;
            Q8=sQuery(id+"F0.wireOp",EDGE,"E6.top");
            var Q9;
            Q9=sQuery(id+"F0.wireOp",EDGE,"E7.top");
            var Q10;
            Q10=sQuery(id+"F0.wireOp",EDGE,"E3.bottom");
            var Q11;
            Q11=sQuery(id+"F0.wireOp",EDGE,"E1.bottom");
            var Q12;
            Q12=sQuery(id+"F0.wireOp",EDGE,"E4.bottom");
            var Q13;
            Q13=sQuery(id+"F0.wireOp",EDGE,"E4.top");
            var Q14;
            Q14=sQuery(id+"F0.wireOp",EDGE,"E3.top");
            var Q15;
            Q15=sQuery(id+"F0.wireOp",EDGE,"E8.top");
            var Q16;
            Q16=sQuery(id+"F0.wireOp",EDGE,"E1.top");
            var Q17;
            Q17=sQuery(id+"F0.wireOp",EDGE,"E2.top");
            var Q18;
            Q18=sQuery(id+"F0.wireOp",EDGE,"E7.left");
            var Q19;
            Q19=sQuery(id+"F0.wireOp",EDGE,"E3.right");
            var Q20;
            Q20=sQuery(id+"F0.wireOp",EDGE,"E6.left");
            var Q21;
            Q21=sQuery(id+"F0.wireOp",EDGE,"E2.right");
            var Q22;
            Q22=sQuery(id+"F0.wireOp",EDGE,"E5.right");
            var Q23;
            Q23=sQuery(id+"F0.wireOp",EDGE,"E8.right");
            var Q24;
            Q24=sQuery(id+"F0.wireOp",EDGE,"E7.right");
            var Q25;
            Q25=sQuery(id+"F0.wireOp",EDGE,"E8.left");
            var Q26;
            Q26=sQuery(id+"F0.wireOp",EDGE,"E5.left");
            var Q27;
            Q27=sQuery(id+"F0.wireOp",EDGE,"E4.left");
            var Q28;
            Q28=sQuery(id+"F0.wireOp",EDGE,"E4.right");
            var Q29;
            Q29=sQuery(id+"F0.wireOp",EDGE,"E6.right");
            var Q30;
            Q30=sQuery(id+"F0.wireOp",EDGE,"E2.left");
            var Q31;
            Q31=sQuery(id+"F0.wireOp",EDGE,"E3.left");
            var Q32;
            Q32=sQuery(id+"F0.wireOp",EDGE,"E1.left");
            var Q33;
            Q33=sQuery(id+"F0.wireOp",EDGE,"E1.right");
            extrude(context, id + "F6", {"entities" : qUnion([Q0]), "surfaceEntities" : qUnion([Q1, Q2, Q3, Q4, Q5, Q6, Q7, Q8, Q9, Q10, Q11, Q12, Q13, Q14, Q15, Q16, Q17, Q18, Q19, Q20, Q21, Q22, Q23, Q24, Q25, Q26, Q27, Q28, Q29, Q30, Q31, Q32, Q33]), "oppositeDirection" : true, "depth" : 25.4 * mm});
        }
    });
